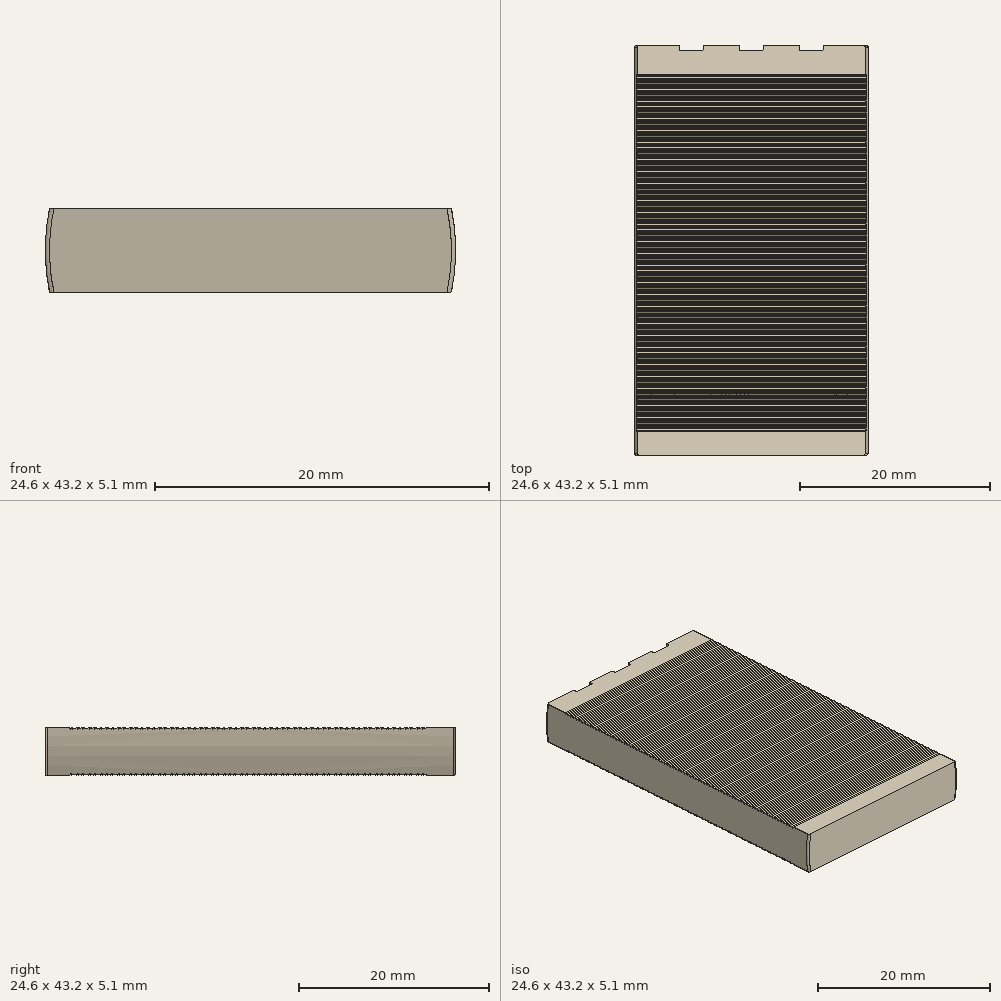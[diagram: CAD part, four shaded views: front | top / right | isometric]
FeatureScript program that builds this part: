
annotation { "Feature Type Name" : "Feature", "Feature Type Description" : "" }
export const myFeature = defineFeature(function(context is Context, id is Id, definition is map)
    precondition{}
    {
        {
            var Q0;
            Q0=qCreatedBy(makeId("Front.planeOp"),FACE);
            var sketch = newSketch(context, id + "F0", { "sketchPlane" : qUnion([Q0])});
            skCircle(sketch, "E0", {"center": v(0, 0) * mm, "radius": 12.32 * mm});
            skSolve(sketch);
        }
        {
            var Q0;
            Q0=qSketchRegion(id+"F0",true);
            extrude(context, id + "F1", {"entities" : qUnion([Q0]), "endBound" : BoundingType.SYMMETRIC, "depth" : 43.18 * mm, "offsetDistance" : 25.4 * mm});
        }
        {
            var Q0;
            Q0=makeQuery(id+"F1.opExtrude","CAP_FACE",FACE,{"disambiguationData":[OSD([sQuery(id+"F0.wireOp",EDGE,"E0")])],"isStart":false});
            var sketch = newSketch(context, id + "F2", { "sketchPlane" : qUnion([Q0])});
            skLineSegment(sketch, "E1.bottom", {"start": v(12.45, 2.54) * mm, "end": v(-12.45, 2.54) * mm});
            skLineSegment(sketch, "E1.top", {"start": v(12.45, -2.54) * mm, "end": v(-12.45, -2.54) * mm});
            skPoint(sketch, "E1.middle", {"position": v(0, 0) * mm});
            skArc(sketch, "E2", {"start": v(-12.45, 2.54) * mm, "mid": v(-12.7, 0) * mm, "end": v(-12.45, -2.54) * mm});
            skArc(sketch, "E3.trimOffspring", {"start": v(12.45, -2.54) * mm, "mid": v(12.7, 0) * mm, "end": v(12.45, 2.54) * mm});
            skSolve(sketch);
        }
        {
            var Q0;
            Q0=qSketchRegion(id+"F2",true);
            extrude(context, id + "F3", {"entities" : qUnion([Q0]), "operationType" : NewBodyOperationType.INTERSECT, "oppositeDirection" : true, "depth" : 50.8 * mm, "offsetDistance" : 25.4 * mm});
        }
        {
            var Q0;
            Q0=qCreatedBy(makeId("Right.planeOp"),FACE);
            var sketch = newSketch(context, id + "F4", { "sketchPlane" : qUnion([Q0])});
            skLineSegment(sketch, "E4", {"start": v(6.35, 2.54) * mm, "end": v(6.22, 2.32) * mm});
            skLineSegment(sketch, "E5", {"start": v(6.22, 2.32) * mm, "end": v(6.1, 2.54) * mm});
            skLineSegment(sketch, "E6.1.0.0", {"start": v(6.1, 2.54) * mm, "end": v(5.97, 2.32) * mm});
            skLineSegment(sketch, "E6.1.0.1", {"start": v(5.97, 2.32) * mm, "end": v(5.84, 2.54) * mm});
            skLineSegment(sketch, "E6.2.0.0", {"start": v(5.84, 2.54) * mm, "end": v(5.72, 2.32) * mm});
            skLineSegment(sketch, "E6.2.0.1", {"start": v(5.72, 2.32) * mm, "end": v(5.59, 2.54) * mm});
            skLineSegment(sketch, "E6.3.0.0", {"start": v(5.59, 2.54) * mm, "end": v(5.46, 2.32) * mm});
            skLineSegment(sketch, "E6.3.0.1", {"start": v(5.46, 2.32) * mm, "end": v(5.33, 2.54) * mm});
            skLineSegment(sketch, "E6.4.0.0", {"start": v(5.33, 2.54) * mm, "end": v(5.2, 2.32) * mm});
            skLineSegment(sketch, "E6.4.0.1", {"start": v(5.2, 2.32) * mm, "end": v(5.08, 2.54) * mm});
            skLineSegment(sketch, "E6.5.0.0", {"start": v(5.08, 2.54) * mm, "end": v(4.95, 2.32) * mm});
            skLineSegment(sketch, "E6.5.0.1", {"start": v(4.95, 2.32) * mm, "end": v(4.83, 2.54) * mm});
            skLineSegment(sketch, "E6.6.0.0", {"start": v(4.83, 2.54) * mm, "end": v(4.7, 2.32) * mm});
            skLineSegment(sketch, "E6.6.0.1", {"start": v(4.7, 2.32) * mm, "end": v(4.57, 2.54) * mm});
            skLineSegment(sketch, "E6.7.0.0", {"start": v(4.57, 2.54) * mm, "end": v(4.45, 2.32) * mm});
            skLineSegment(sketch, "E6.7.0.1", {"start": v(4.45, 2.32) * mm, "end": v(4.32, 2.54) * mm});
            skLineSegment(sketch, "E6.8.0.0", {"start": v(4.32, 2.54) * mm, "end": v(4.2, 2.32) * mm});
            skLineSegment(sketch, "E6.8.0.1", {"start": v(4.2, 2.32) * mm, "end": v(4.06, 2.54) * mm});
            skLineSegment(sketch, "E6.9.0.0", {"start": v(4.06, 2.54) * mm, "end": v(3.94, 2.32) * mm});
            skLineSegment(sketch, "E6.9.0.1", {"start": v(3.94, 2.32) * mm, "end": v(3.81, 2.54) * mm});
            skLineSegment(sketch, "E6.10.0.0", {"start": v(3.81, 2.54) * mm, "end": v(3.68, 2.32) * mm});
            skLineSegment(sketch, "E6.10.0.1", {"start": v(3.68, 2.32) * mm, "end": v(3.56, 2.54) * mm});
            skLineSegment(sketch, "E6.11.0.0", {"start": v(3.56, 2.54) * mm, "end": v(3.43, 2.32) * mm});
            skLineSegment(sketch, "E6.11.0.1", {"start": v(3.43, 2.32) * mm, "end": v(3.3, 2.54) * mm});
            skLineSegment(sketch, "E6.12.0.0", {"start": v(3.3, 2.54) * mm, "end": v(3.18, 2.32) * mm});
            skLineSegment(sketch, "E6.12.0.1", {"start": v(3.17, 2.32) * mm, "end": v(3.05, 2.54) * mm});
            skLineSegment(sketch, "E6.13.0.0", {"start": v(3.05, 2.54) * mm, "end": v(2.92, 2.32) * mm});
            skLineSegment(sketch, "E6.13.0.1", {"start": v(2.92, 2.32) * mm, "end": v(2.8, 2.54) * mm});
            skLineSegment(sketch, "E6.14.0.0", {"start": v(2.8, 2.54) * mm, "end": v(2.67, 2.32) * mm});
            skLineSegment(sketch, "E6.14.0.1", {"start": v(2.67, 2.32) * mm, "end": v(2.54, 2.54) * mm});
            skLineSegment(sketch, "E6.15.0.0", {"start": v(2.54, 2.54) * mm, "end": v(2.41, 2.32) * mm});
            skLineSegment(sketch, "E6.15.0.1", {"start": v(2.41, 2.32) * mm, "end": v(2.29, 2.54) * mm});
            skLineSegment(sketch, "E6.16.0.0", {"start": v(2.29, 2.54) * mm, "end": v(2.16, 2.32) * mm});
            skLineSegment(sketch, "E6.16.0.1", {"start": v(2.16, 2.32) * mm, "end": v(2.03, 2.54) * mm});
            skLineSegment(sketch, "E6.17.0.0", {"start": v(2.03, 2.54) * mm, "end": v(1.9, 2.32) * mm});
            skLineSegment(sketch, "E6.17.0.1", {"start": v(1.9, 2.32) * mm, "end": v(1.78, 2.54) * mm});
            skLineSegment(sketch, "E6.18.0.0", {"start": v(1.78, 2.54) * mm, "end": v(1.65, 2.32) * mm});
            skLineSegment(sketch, "E6.18.0.1", {"start": v(1.65, 2.32) * mm, "end": v(1.52, 2.54) * mm});
            skLineSegment(sketch, "E6.19.0.0", {"start": v(1.52, 2.54) * mm, "end": v(1.4, 2.32) * mm});
            skLineSegment(sketch, "E6.19.0.1", {"start": v(1.4, 2.32) * mm, "end": v(1.27, 2.54) * mm});
            skLineSegment(sketch, "E6.20.0.0", {"start": v(1.27, 2.54) * mm, "end": v(1.14, 2.32) * mm});
            skLineSegment(sketch, "E6.20.0.1", {"start": v(1.14, 2.32) * mm, "end": v(1.02, 2.54) * mm});
            skLineSegment(sketch, "E6.21.0.0", {"start": v(1.02, 2.54) * mm, "end": v(0.89, 2.32) * mm});
            skLineSegment(sketch, "E6.21.0.1", {"start": v(0.89, 2.32) * mm, "end": v(0.76, 2.54) * mm});
            skLineSegment(sketch, "E6.22.0.0", {"start": v(0.76, 2.54) * mm, "end": v(0.63, 2.32) * mm});
            skLineSegment(sketch, "E6.22.0.1", {"start": v(0.63, 2.32) * mm, "end": v(0.5, 2.54) * mm});
            skLineSegment(sketch, "E6.23.0.0", {"start": v(0.5, 2.54) * mm, "end": v(0.38, 2.32) * mm});
            skLineSegment(sketch, "E6.23.0.1", {"start": v(0.38, 2.32) * mm, "end": v(0.25, 2.54) * mm});
            skLineSegment(sketch, "E6.24.0.0", {"start": v(0.25, 2.54) * mm, "end": v(0.13, 2.32) * mm});
            skLineSegment(sketch, "E6.24.0.1", {"start": v(0.13, 2.32) * mm, "end": v(0, 2.54) * mm});
            skLineSegment(sketch, "E6.25.0.0", {"start": v(0, 2.54) * mm, "end": v(-0.13, 2.32) * mm});
            skLineSegment(sketch, "E6.25.0.1", {"start": v(-0.13, 2.32) * mm, "end": v(-0.25, 2.54) * mm});
            skLineSegment(sketch, "E6.26.0.0", {"start": v(-0.25, 2.54) * mm, "end": v(-0.38, 2.32) * mm});
            skLineSegment(sketch, "E6.26.0.1", {"start": v(-0.38, 2.32) * mm, "end": v(-0.5, 2.54) * mm});
            skLineSegment(sketch, "E6.27.0.0", {"start": v(-0.5, 2.54) * mm, "end": v(-0.64, 2.32) * mm});
            skLineSegment(sketch, "E6.27.0.1", {"start": v(-0.64, 2.32) * mm, "end": v(-0.76, 2.54) * mm});
            skLineSegment(sketch, "E6.28.0.0", {"start": v(-0.76, 2.54) * mm, "end": v(-0.89, 2.32) * mm});
            skLineSegment(sketch, "E6.28.0.1", {"start": v(-0.89, 2.32) * mm, "end": v(-1.02, 2.54) * mm});
            skLineSegment(sketch, "E6.29.0.0", {"start": v(-1.02, 2.54) * mm, "end": v(-1.14, 2.32) * mm});
            skLineSegment(sketch, "E6.29.0.1", {"start": v(-1.14, 2.32) * mm, "end": v(-1.27, 2.54) * mm});
            skLineSegment(sketch, "E6.30.0.0", {"start": v(-1.27, 2.54) * mm, "end": v(-1.4, 2.32) * mm});
            skLineSegment(sketch, "E6.30.0.1", {"start": v(-1.4, 2.32) * mm, "end": v(-1.52, 2.54) * mm});
            skLineSegment(sketch, "E6.31.0.0", {"start": v(-1.52, 2.54) * mm, "end": v(-1.65, 2.32) * mm});
            skLineSegment(sketch, "E6.31.0.1", {"start": v(-1.65, 2.32) * mm, "end": v(-1.78, 2.54) * mm});
            skLineSegment(sketch, "E6.32.0.0", {"start": v(-1.78, 2.54) * mm, "end": v(-1.9, 2.32) * mm});
            skLineSegment(sketch, "E6.32.0.1", {"start": v(-1.9, 2.32) * mm, "end": v(-2.03, 2.54) * mm});
            skLineSegment(sketch, "E6.33.0.0", {"start": v(-2.03, 2.54) * mm, "end": v(-2.16, 2.32) * mm});
            skLineSegment(sketch, "E6.33.0.1", {"start": v(-2.16, 2.32) * mm, "end": v(-2.29, 2.54) * mm});
            skLineSegment(sketch, "E6.34.0.0", {"start": v(-2.29, 2.54) * mm, "end": v(-2.41, 2.32) * mm});
            skLineSegment(sketch, "E6.34.0.1", {"start": v(-2.41, 2.32) * mm, "end": v(-2.54, 2.54) * mm});
            skLineSegment(sketch, "E6.35.0.0", {"start": v(-2.54, 2.54) * mm, "end": v(-2.67, 2.32) * mm});
            skLineSegment(sketch, "E6.35.0.1", {"start": v(-2.67, 2.32) * mm, "end": v(-2.8, 2.54) * mm});
            skLineSegment(sketch, "E6.36.0.0", {"start": v(-2.8, 2.54) * mm, "end": v(-2.92, 2.32) * mm});
            skLineSegment(sketch, "E6.36.0.1", {"start": v(-2.92, 2.32) * mm, "end": v(-3.05, 2.54) * mm});
            skLineSegment(sketch, "E6.37.0.0", {"start": v(-3.05, 2.54) * mm, "end": v(-3.18, 2.32) * mm});
            skLineSegment(sketch, "E6.37.0.1", {"start": v(-3.18, 2.32) * mm, "end": v(-3.3, 2.54) * mm});
            skLineSegment(sketch, "E6.38.0.0", {"start": v(-3.3, 2.54) * mm, "end": v(-3.43, 2.32) * mm});
            skLineSegment(sketch, "E6.38.0.1", {"start": v(-3.43, 2.32) * mm, "end": v(-3.56, 2.54) * mm});
            skLineSegment(sketch, "E6.39.0.0", {"start": v(-3.56, 2.54) * mm, "end": v(-3.68, 2.32) * mm});
            skLineSegment(sketch, "E6.39.0.1", {"start": v(-3.68, 2.32) * mm, "end": v(-3.81, 2.54) * mm});
            skLineSegment(sketch, "E6.40.0.0", {"start": v(-3.81, 2.54) * mm, "end": v(-3.94, 2.32) * mm});
            skLineSegment(sketch, "E6.40.0.1", {"start": v(-3.94, 2.32) * mm, "end": v(-4.06, 2.54) * mm});
            skLineSegment(sketch, "E6.41.0.0", {"start": v(-4.06, 2.54) * mm, "end": v(-4.2, 2.32) * mm});
            skLineSegment(sketch, "E6.41.0.1", {"start": v(-4.2, 2.32) * mm, "end": v(-4.32, 2.54) * mm});
            skLineSegment(sketch, "E6.42.0.0", {"start": v(-4.32, 2.54) * mm, "end": v(-4.45, 2.32) * mm});
            skLineSegment(sketch, "E6.42.0.1", {"start": v(-4.45, 2.32) * mm, "end": v(-4.57, 2.54) * mm});
            skLineSegment(sketch, "E6.43.0.0", {"start": v(-4.57, 2.54) * mm, "end": v(-4.7, 2.32) * mm});
            skLineSegment(sketch, "E6.43.0.1", {"start": v(-4.7, 2.32) * mm, "end": v(-4.83, 2.54) * mm});
            skLineSegment(sketch, "E6.44.0.0", {"start": v(-4.83, 2.54) * mm, "end": v(-4.95, 2.32) * mm});
            skLineSegment(sketch, "E6.44.0.1", {"start": v(-4.95, 2.32) * mm, "end": v(-5.08, 2.54) * mm});
            skLineSegment(sketch, "E6.45.0.0", {"start": v(-5.08, 2.54) * mm, "end": v(-5.2, 2.32) * mm});
            skLineSegment(sketch, "E6.45.0.1", {"start": v(-5.2, 2.32) * mm, "end": v(-5.33, 2.54) * mm});
            skLineSegment(sketch, "E6.46.0.0", {"start": v(-5.33, 2.54) * mm, "end": v(-5.46, 2.32) * mm});
            skLineSegment(sketch, "E6.46.0.1", {"start": v(-5.46, 2.32) * mm, "end": v(-5.59, 2.54) * mm});
            skLineSegment(sketch, "E6.47.0.0", {"start": v(-5.59, 2.54) * mm, "end": v(-5.72, 2.32) * mm});
            skLineSegment(sketch, "E6.47.0.1", {"start": v(-5.72, 2.32) * mm, "end": v(-5.84, 2.54) * mm});
            skLineSegment(sketch, "E6.48.0.0", {"start": v(-5.84, 2.54) * mm, "end": v(-5.97, 2.32) * mm});
            skLineSegment(sketch, "E6.48.0.1", {"start": v(-5.97, 2.32) * mm, "end": v(-6.1, 2.54) * mm});
            skLineSegment(sketch, "E6.49.0.0", {"start": v(-6.1, 2.54) * mm, "end": v(-6.22, 2.32) * mm});
            skLineSegment(sketch, "E6.49.0.1", {"start": v(-6.22, 2.32) * mm, "end": v(-6.35, 2.54) * mm});
            skLineSegment(sketch, "E6.50.0.0", {"start": v(-6.35, 2.54) * mm, "end": v(-6.48, 2.32) * mm});
            skLineSegment(sketch, "E6.50.0.1", {"start": v(-6.48, 2.32) * mm, "end": v(-6.6, 2.54) * mm});
            skLineSegment(sketch, "E6.51.0.0", {"start": v(-6.6, 2.54) * mm, "end": v(-6.73, 2.32) * mm});
            skLineSegment(sketch, "E6.51.0.1", {"start": v(-6.73, 2.32) * mm, "end": v(-6.86, 2.54) * mm});
            skLineSegment(sketch, "E6.52.0.0", {"start": v(-6.86, 2.54) * mm, "end": v(-6.99, 2.32) * mm});
            skLineSegment(sketch, "E6.52.0.1", {"start": v(-6.99, 2.32) * mm, "end": v(-7.11, 2.54) * mm});
            skLineSegment(sketch, "E6.53.0.0", {"start": v(-7.11, 2.54) * mm, "end": v(-7.24, 2.32) * mm});
            skLineSegment(sketch, "E6.53.0.1", {"start": v(-7.24, 2.32) * mm, "end": v(-7.37, 2.54) * mm});
            skLineSegment(sketch, "E6.54.0.0", {"start": v(-7.37, 2.54) * mm, "end": v(-7.5, 2.32) * mm});
            skLineSegment(sketch, "E6.54.0.1", {"start": v(-7.5, 2.32) * mm, "end": v(-7.62, 2.54) * mm});
            skLineSegment(sketch, "E6.55.0.0", {"start": v(-7.62, 2.54) * mm, "end": v(-7.75, 2.32) * mm});
            skLineSegment(sketch, "E6.55.0.1", {"start": v(-7.75, 2.32) * mm, "end": v(-7.87, 2.54) * mm});
            skLineSegment(sketch, "E6.56.0.0", {"start": v(-7.87, 2.54) * mm, "end": v(-8, 2.32) * mm});
            skLineSegment(sketch, "E6.56.0.1", {"start": v(-8, 2.32) * mm, "end": v(-8.13, 2.54) * mm});
            skLineSegment(sketch, "E6.57.0.0", {"start": v(-8.13, 2.54) * mm, "end": v(-8.26, 2.32) * mm});
            skLineSegment(sketch, "E6.57.0.1", {"start": v(-8.26, 2.32) * mm, "end": v(-8.38, 2.54) * mm});
            skLineSegment(sketch, "E6.58.0.0", {"start": v(-8.38, 2.54) * mm, "end": v(-8.5, 2.32) * mm});
            skLineSegment(sketch, "E6.58.0.1", {"start": v(-8.5, 2.32) * mm, "end": v(-8.64, 2.54) * mm});
            skLineSegment(sketch, "E6.59.0.0", {"start": v(-8.64, 2.54) * mm, "end": v(-8.76, 2.32) * mm});
            skLineSegment(sketch, "E6.59.0.1", {"start": v(-8.76, 2.32) * mm, "end": v(-8.9, 2.54) * mm});
            skLineSegment(sketch, "E6.60.0.0", {"start": v(-8.9, 2.54) * mm, "end": v(-9.02, 2.32) * mm});
            skLineSegment(sketch, "E6.60.0.1", {"start": v(-9.02, 2.32) * mm, "end": v(-9.14, 2.54) * mm});
            skLineSegment(sketch, "E6.61.0.0", {"start": v(-9.14, 2.54) * mm, "end": v(-9.27, 2.32) * mm});
            skLineSegment(sketch, "E6.61.0.1", {"start": v(-9.27, 2.32) * mm, "end": v(-9.4, 2.54) * mm});
            skLineSegment(sketch, "E6.62.0.0", {"start": v(-9.4, 2.54) * mm, "end": v(-9.53, 2.32) * mm});
            skLineSegment(sketch, "E6.62.0.1", {"start": v(-9.53, 2.32) * mm, "end": v(-9.65, 2.54) * mm});
            skLineSegment(sketch, "E6.63.0.0", {"start": v(-9.65, 2.54) * mm, "end": v(-9.78, 2.32) * mm});
            skLineSegment(sketch, "E6.63.0.1", {"start": v(-9.78, 2.32) * mm, "end": v(-9.9, 2.54) * mm});
            skLineSegment(sketch, "E6.64.0.0", {"start": v(-9.9, 2.54) * mm, "end": v(-10.03, 2.32) * mm});
            skLineSegment(sketch, "E6.64.0.1", {"start": v(-10.03, 2.32) * mm, "end": v(-10.16, 2.54) * mm});
            skLineSegment(sketch, "E6.65.0.0", {"start": v(-10.16, 2.54) * mm, "end": v(-10.29, 2.32) * mm});
            skLineSegment(sketch, "E6.65.0.1", {"start": v(-10.29, 2.32) * mm, "end": v(-10.41, 2.54) * mm});
            skLineSegment(sketch, "E6.66.0.0", {"start": v(-10.41, 2.54) * mm, "end": v(-10.54, 2.32) * mm});
            skLineSegment(sketch, "E6.66.0.1", {"start": v(-10.54, 2.32) * mm, "end": v(-10.67, 2.54) * mm});
            skLineSegment(sketch, "E6.67.0.0", {"start": v(-10.67, 2.54) * mm, "end": v(-10.8, 2.32) * mm});
            skLineSegment(sketch, "E6.67.0.1", {"start": v(-10.8, 2.32) * mm, "end": v(-10.92, 2.54) * mm});
            skLineSegment(sketch, "E6.68.0.0", {"start": v(-10.92, 2.54) * mm, "end": v(-11.05, 2.32) * mm});
            skLineSegment(sketch, "E6.68.0.1", {"start": v(-11.05, 2.32) * mm, "end": v(-11.18, 2.54) * mm});
            skLineSegment(sketch, "E6.69.0.0", {"start": v(-11.18, 2.54) * mm, "end": v(-11.3, 2.32) * mm});
            skLineSegment(sketch, "E6.69.0.1", {"start": v(-11.3, 2.32) * mm, "end": v(-11.43, 2.54) * mm});
            skLineSegment(sketch, "E6.70.0.0", {"start": v(-11.43, 2.54) * mm, "end": v(-11.56, 2.32) * mm});
            skLineSegment(sketch, "E6.70.0.1", {"start": v(-11.56, 2.32) * mm, "end": v(-11.68, 2.54) * mm});
            skLineSegment(sketch, "E6.71.0.0", {"start": v(-11.68, 2.54) * mm, "end": v(-11.81, 2.32) * mm});
            skLineSegment(sketch, "E6.71.0.1", {"start": v(-11.81, 2.32) * mm, "end": v(-11.94, 2.54) * mm});
            skLineSegment(sketch, "E6.72.0.0", {"start": v(-11.94, 2.54) * mm, "end": v(-12.07, 2.32) * mm});
            skLineSegment(sketch, "E6.72.0.1", {"start": v(-12.07, 2.32) * mm, "end": v(-12.2, 2.54) * mm});
            skLineSegment(sketch, "E6.73.0.0", {"start": v(-12.2, 2.54) * mm, "end": v(-12.32, 2.32) * mm});
            skLineSegment(sketch, "E6.73.0.1", {"start": v(-12.32, 2.32) * mm, "end": v(-12.45, 2.54) * mm});
            skLineSegment(sketch, "E6.74.0.0", {"start": v(-12.45, 2.54) * mm, "end": v(-12.57, 2.32) * mm});
            skLineSegment(sketch, "E6.74.0.1", {"start": v(-12.57, 2.32) * mm, "end": v(-12.7, 2.54) * mm});
            skLineSegment(sketch, "E6.75.0.0", {"start": v(-12.7, 2.54) * mm, "end": v(-12.83, 2.32) * mm});
            skLineSegment(sketch, "E6.75.0.1", {"start": v(-12.83, 2.32) * mm, "end": v(-12.95, 2.54) * mm});
            skLineSegment(sketch, "E6.76.0.0", {"start": v(-12.95, 2.54) * mm, "end": v(-13.08, 2.32) * mm});
            skLineSegment(sketch, "E6.76.0.1", {"start": v(-13.08, 2.32) * mm, "end": v(-13.2, 2.54) * mm});
            skLineSegment(sketch, "E6.77.0.0", {"start": v(-13.2, 2.54) * mm, "end": v(-13.34, 2.32) * mm});
            skLineSegment(sketch, "E6.77.0.1", {"start": v(-13.34, 2.32) * mm, "end": v(-13.46, 2.54) * mm});
            skLineSegment(sketch, "E6.78.0.0", {"start": v(-13.46, 2.54) * mm, "end": v(-13.59, 2.32) * mm});
            skLineSegment(sketch, "E6.78.0.1", {"start": v(-13.59, 2.32) * mm, "end": v(-13.72, 2.54) * mm});
            skLineSegment(sketch, "E6.79.0.0", {"start": v(-13.72, 2.54) * mm, "end": v(-13.84, 2.32) * mm});
            skLineSegment(sketch, "E6.79.0.1", {"start": v(-13.84, 2.32) * mm, "end": v(-13.97, 2.54) * mm});
            skLineSegment(sketch, "E6.80.0.0", {"start": v(-13.97, 2.54) * mm, "end": v(-14.1, 2.32) * mm});
            skLineSegment(sketch, "E6.80.0.1", {"start": v(-14.1, 2.32) * mm, "end": v(-14.22, 2.54) * mm});
            skLineSegment(sketch, "E6.81.0.0", {"start": v(-14.22, 2.54) * mm, "end": v(-14.35, 2.32) * mm});
            skLineSegment(sketch, "E6.81.0.1", {"start": v(-14.35, 2.32) * mm, "end": v(-14.48, 2.54) * mm});
            skLineSegment(sketch, "E6.82.0.0", {"start": v(-14.48, 2.54) * mm, "end": v(-14.6, 2.32) * mm});
            skLineSegment(sketch, "E6.82.0.1", {"start": v(-14.6, 2.32) * mm, "end": v(-14.73, 2.54) * mm});
            skLineSegment(sketch, "E6.83.0.0", {"start": v(-14.73, 2.54) * mm, "end": v(-14.86, 2.32) * mm});
            skLineSegment(sketch, "E6.83.0.1", {"start": v(-14.86, 2.32) * mm, "end": v(-14.99, 2.54) * mm});
            skLineSegment(sketch, "E6.84.0.0", {"start": v(-14.99, 2.54) * mm, "end": v(-15.11, 2.32) * mm});
            skLineSegment(sketch, "E6.84.0.1", {"start": v(-15.11, 2.32) * mm, "end": v(-15.24, 2.54) * mm});
            skLineSegment(sketch, "E6.85.0.0", {"start": v(-15.24, 2.54) * mm, "end": v(-15.37, 2.32) * mm});
            skLineSegment(sketch, "E6.85.0.1", {"start": v(-15.37, 2.32) * mm, "end": v(-15.5, 2.54) * mm});
            skLineSegment(sketch, "E6.86.0.0", {"start": v(-15.5, 2.54) * mm, "end": v(-15.62, 2.32) * mm});
            skLineSegment(sketch, "E6.86.0.1", {"start": v(-15.62, 2.32) * mm, "end": v(-15.75, 2.54) * mm});
            skLineSegment(sketch, "E6.87.0.0", {"start": v(-15.75, 2.54) * mm, "end": v(-15.88, 2.32) * mm});
            skLineSegment(sketch, "E6.87.0.1", {"start": v(-15.88, 2.32) * mm, "end": v(-16, 2.54) * mm});
            skLineSegment(sketch, "E6.88.0.0", {"start": v(-16, 2.54) * mm, "end": v(-16.13, 2.32) * mm});
            skLineSegment(sketch, "E6.88.0.1", {"start": v(-16.13, 2.32) * mm, "end": v(-16.26, 2.54) * mm});
            skLineSegment(sketch, "E6.89.0.0", {"start": v(-16.26, 2.54) * mm, "end": v(-16.38, 2.32) * mm});
            skLineSegment(sketch, "E6.89.0.1", {"start": v(-16.38, 2.32) * mm, "end": v(-16.51, 2.54) * mm});
            skLineSegment(sketch, "E6.90.0.0", {"start": v(-16.51, 2.54) * mm, "end": v(-16.64, 2.32) * mm});
            skLineSegment(sketch, "E6.90.0.1", {"start": v(-16.64, 2.32) * mm, "end": v(-16.76, 2.54) * mm});
            skLineSegment(sketch, "E6.91.0.0", {"start": v(-16.76, 2.54) * mm, "end": v(-16.9, 2.32) * mm});
            skLineSegment(sketch, "E6.91.0.1", {"start": v(-16.9, 2.32) * mm, "end": v(-17.02, 2.54) * mm});
            skLineSegment(sketch, "E6.92.0.0", {"start": v(-17.02, 2.54) * mm, "end": v(-17.15, 2.32) * mm});
            skLineSegment(sketch, "E6.92.0.1", {"start": v(-17.15, 2.32) * mm, "end": v(-17.27, 2.54) * mm});
            skLineSegment(sketch, "E6.93.0.0", {"start": v(-17.27, 2.54) * mm, "end": v(-17.4, 2.32) * mm});
            skLineSegment(sketch, "E6.93.0.1", {"start": v(-17.4, 2.32) * mm, "end": v(-17.53, 2.54) * mm});
            skLineSegment(sketch, "E6.94.0.0", {"start": v(-17.53, 2.54) * mm, "end": v(-17.65, 2.32) * mm});
            skLineSegment(sketch, "E6.94.0.1", {"start": v(-17.65, 2.32) * mm, "end": v(-17.78, 2.54) * mm});
            skLineSegment(sketch, "E6.95.0.0", {"start": v(-17.78, 2.54) * mm, "end": v(-17.9, 2.32) * mm});
            skLineSegment(sketch, "E6.95.0.1", {"start": v(-17.9, 2.32) * mm, "end": v(-18.03, 2.54) * mm});
            skLineSegment(sketch, "E6.96.0.0", {"start": v(-18.03, 2.54) * mm, "end": v(-18.16, 2.32) * mm});
            skLineSegment(sketch, "E6.96.0.1", {"start": v(-18.16, 2.32) * mm, "end": v(-18.29, 2.54) * mm});
            skLineSegment(sketch, "E6.97.0.0", {"start": v(-18.29, 2.54) * mm, "end": v(-18.42, 2.32) * mm});
            skLineSegment(sketch, "E6.97.0.1", {"start": v(-18.42, 2.32) * mm, "end": v(-18.54, 2.54) * mm});
            skLineSegment(sketch, "E6.98.0.0", {"start": v(-18.54, 2.54) * mm, "end": v(-18.67, 2.32) * mm});
            skLineSegment(sketch, "E6.98.0.1", {"start": v(-18.67, 2.32) * mm, "end": v(-18.8, 2.54) * mm});
            skLineSegment(sketch, "E6.99.0.0", {"start": v(-18.8, 2.54) * mm, "end": v(-18.92, 2.32) * mm});
            skLineSegment(sketch, "E6.99.0.1", {"start": v(-18.92, 2.32) * mm, "end": v(-19.05, 2.54) * mm});
            skLineSegment(sketch, "E6.direction1", {"start": v(6.22, -2.33) * mm, "end": v(5.97, -2.33) * mm, "construction": true});
            skLineSegment(sketch, "E7", {"start": v(-19.05, 2.6) * mm, "end": v(-19.05, 2.54) * mm});
            skLineSegment(sketch, "E8.MirrorCS", {"start": v(6.22, -2.33) * mm, "end": v(6.1, -2.55) * mm});
            skLineSegment(sketch, "E9.MirrorCS", {"start": v(6.35, -2.55) * mm, "end": v(6.22, -2.33) * mm});
            skLineSegment(sketch, "E10.MirrorCS", {"start": v(5.97, -2.33) * mm, "end": v(5.84, -2.55) * mm});
            skLineSegment(sketch, "E11.MirrorCS", {"start": v(-19.05, -2.6) * mm, "end": v(-19.05, -2.55) * mm});
            skLineSegment(sketch, "E12.MirrorCS", {"start": v(6.1, -2.55) * mm, "end": v(5.97, -2.33) * mm});
            skLineSegment(sketch, "E13.MirrorCS", {"start": v(-11.05, -2.33) * mm, "end": v(-11.18, -2.55) * mm});
            skLineSegment(sketch, "E14.MirrorCS", {"start": v(4.83, -2.55) * mm, "end": v(4.7, -2.33) * mm});
            skLineSegment(sketch, "E15.MirrorCS", {"start": v(-2.29, -2.55) * mm, "end": v(-2.41, -2.33) * mm});
            skLineSegment(sketch, "E16.MirrorCS", {"start": v(-18.54, -2.55) * mm, "end": v(-18.67, -2.33) * mm});
            skLineSegment(sketch, "E17.MirrorCS", {"start": v(-14.48, -2.55) * mm, "end": v(-14.6, -2.33) * mm});
            skLineSegment(sketch, "E18.MirrorCS", {"start": v(-16.76, -2.55) * mm, "end": v(-16.9, -2.33) * mm});
            skLineSegment(sketch, "E19.MirrorCS", {"start": v(-0.64, -2.33) * mm, "end": v(-0.76, -2.55) * mm});
            skLineSegment(sketch, "E20.MirrorCS", {"start": v(-8.76, -2.33) * mm, "end": v(-8.9, -2.55) * mm});
            skLineSegment(sketch, "E21.MirrorCS", {"start": v(-2.67, -2.33) * mm, "end": v(-2.8, -2.55) * mm});
            skLineSegment(sketch, "E22.MirrorCS", {"start": v(-15.11, -2.33) * mm, "end": v(-15.24, -2.55) * mm});
            skLineSegment(sketch, "E23.MirrorCS", {"start": v(2.29, -2.55) * mm, "end": v(2.16, -2.33) * mm});
            skLineSegment(sketch, "E24.MirrorCS", {"start": v(-14.99, -2.55) * mm, "end": v(-15.11, -2.33) * mm});
            skLineSegment(sketch, "E25.MirrorCS", {"start": v(-11.68, -2.55) * mm, "end": v(-11.81, -2.33) * mm});
            skLineSegment(sketch, "E26.MirrorCS", {"start": v(2.8, -2.55) * mm, "end": v(2.67, -2.33) * mm});
            skLineSegment(sketch, "E27.MirrorCS", {"start": v(2.03, -2.55) * mm, "end": v(1.9, -2.33) * mm});
            skLineSegment(sketch, "E28.MirrorCS", {"start": v(-3.43, -2.33) * mm, "end": v(-3.56, -2.55) * mm});
            skLineSegment(sketch, "E29.MirrorCS", {"start": v(-2.16, -2.33) * mm, "end": v(-2.29, -2.55) * mm});
            skLineSegment(sketch, "E30.MirrorCS", {"start": v(-14.35, -2.33) * mm, "end": v(-14.48, -2.55) * mm});
            skLineSegment(sketch, "E31.MirrorCS", {"start": v(-12.7, -2.55) * mm, "end": v(-12.83, -2.33) * mm});
            skLineSegment(sketch, "E32.MirrorCS", {"start": v(-8.38, -2.55) * mm, "end": v(-8.5, -2.33) * mm});
            skLineSegment(sketch, "E33.MirrorCS", {"start": v(-11.56, -2.33) * mm, "end": v(-11.68, -2.55) * mm});
            skLineSegment(sketch, "E34.MirrorCS", {"start": v(-17.65, -2.33) * mm, "end": v(-17.78, -2.55) * mm});
            skLineSegment(sketch, "E35.MirrorCS", {"start": v(-12.32, -2.33) * mm, "end": v(-12.45, -2.55) * mm});
            skLineSegment(sketch, "E36.MirrorCS", {"start": v(2.16, -2.33) * mm, "end": v(2.03, -2.55) * mm});
            skLineSegment(sketch, "E37.MirrorCS", {"start": v(-2.8, -2.55) * mm, "end": v(-2.92, -2.33) * mm});
            skLineSegment(sketch, "E38.MirrorCS", {"start": v(-4.57, -2.55) * mm, "end": v(-4.7, -2.33) * mm});
            skLineSegment(sketch, "E39.MirrorCS", {"start": v(-1.02, -2.55) * mm, "end": v(-1.14, -2.33) * mm});
            skLineSegment(sketch, "E40.MirrorCS", {"start": v(4.95, -2.33) * mm, "end": v(4.83, -2.55) * mm});
            skLineSegment(sketch, "E41.MirrorCS", {"start": v(5.08, -2.55) * mm, "end": v(4.95, -2.33) * mm});
            skLineSegment(sketch, "E42.MirrorCS", {"start": v(-13.46, -2.55) * mm, "end": v(-13.59, -2.33) * mm});
            skLineSegment(sketch, "E43.MirrorCS", {"start": v(-13.08, -2.33) * mm, "end": v(-13.2, -2.55) * mm});
            skLineSegment(sketch, "E44.MirrorCS", {"start": v(-5.59, -2.55) * mm, "end": v(-5.72, -2.33) * mm});
            skLineSegment(sketch, "E45.MirrorCS", {"start": v(-5.33, -2.55) * mm, "end": v(-5.46, -2.33) * mm});
            skLineSegment(sketch, "E46.MirrorCS", {"start": v(4.45, -2.33) * mm, "end": v(4.32, -2.55) * mm});
            skLineSegment(sketch, "E47.MirrorCS", {"start": v(-3.56, -2.55) * mm, "end": v(-3.68, -2.33) * mm});
            skLineSegment(sketch, "E48.MirrorCS", {"start": v(-15.24, -2.55) * mm, "end": v(-15.37, -2.33) * mm});
            skLineSegment(sketch, "E49.MirrorCS", {"start": v(-6.99, -2.33) * mm, "end": v(-7.11, -2.55) * mm});
            skLineSegment(sketch, "E50.MirrorCS", {"start": v(-2.54, -2.55) * mm, "end": v(-2.67, -2.33) * mm});
            skLineSegment(sketch, "E51.MirrorCS", {"start": v(-12.45, -2.55) * mm, "end": v(-12.57, -2.33) * mm});
            skLineSegment(sketch, "E52.MirrorCS", {"start": v(-16.9, -2.33) * mm, "end": v(-17.02, -2.55) * mm});
            skLineSegment(sketch, "E53.MirrorCS", {"start": v(-3.05, -2.55) * mm, "end": v(-3.18, -2.33) * mm});
            skLineSegment(sketch, "E54.MirrorCS", {"start": v(3.81, -2.55) * mm, "end": v(3.68, -2.33) * mm});
            skLineSegment(sketch, "E55.MirrorCS", {"start": v(-10.67, -2.55) * mm, "end": v(-10.8, -2.33) * mm});
            skLineSegment(sketch, "E56.MirrorCS", {"start": v(-14.22, -2.55) * mm, "end": v(-14.35, -2.33) * mm});
            skLineSegment(sketch, "E57.MirrorCS", {"start": v(-3.94, -2.33) * mm, "end": v(-4.06, -2.55) * mm});
            skLineSegment(sketch, "E58.MirrorCS", {"start": v(-14.1, -2.33) * mm, "end": v(-14.22, -2.55) * mm});
            skLineSegment(sketch, "E59.MirrorCS", {"start": v(-15.5, -2.55) * mm, "end": v(-15.62, -2.33) * mm});
            skLineSegment(sketch, "E60.MirrorCS", {"start": v(3.05, -2.55) * mm, "end": v(2.92, -2.33) * mm});
            skLineSegment(sketch, "E61.MirrorCS", {"start": v(-10.03, -2.33) * mm, "end": v(-10.16, -2.55) * mm});
            skLineSegment(sketch, "E62.MirrorCS", {"start": v(5.84, -2.55) * mm, "end": v(5.72, -2.33) * mm});
            skLineSegment(sketch, "E63.MirrorCS", {"start": v(3.68, -2.33) * mm, "end": v(3.56, -2.55) * mm});
            skLineSegment(sketch, "E64.MirrorCS", {"start": v(-17.53, -2.55) * mm, "end": v(-17.65, -2.33) * mm});
            skLineSegment(sketch, "E65.MirrorCS", {"start": v(1.65, -2.33) * mm, "end": v(1.52, -2.55) * mm});
            skLineSegment(sketch, "E66.MirrorCS", {"start": v(-17.15, -2.33) * mm, "end": v(-17.27, -2.55) * mm});
            skLineSegment(sketch, "E67.MirrorCS", {"start": v(-16.51, -2.55) * mm, "end": v(-16.64, -2.33) * mm});
            skLineSegment(sketch, "E68.MirrorCS", {"start": v(-0.5, -2.55) * mm, "end": v(-0.64, -2.33) * mm});
            skLineSegment(sketch, "E69.MirrorCS", {"start": v(-1.78, -2.55) * mm, "end": v(-1.9, -2.33) * mm});
            skLineSegment(sketch, "E70.MirrorCS", {"start": v(2.92, -2.33) * mm, "end": v(2.8, -2.55) * mm});
            skLineSegment(sketch, "E71.MirrorCS", {"start": v(1.78, -2.55) * mm, "end": v(1.65, -2.33) * mm});
            skLineSegment(sketch, "E72.MirrorCS", {"start": v(-11.94, -2.55) * mm, "end": v(-12.07, -2.33) * mm});
            skLineSegment(sketch, "E73.MirrorCS", {"start": v(-8, -2.33) * mm, "end": v(-8.13, -2.55) * mm});
            skLineSegment(sketch, "E74.MirrorCS", {"start": v(-5.97, -2.33) * mm, "end": v(-6.1, -2.55) * mm});
            skLineSegment(sketch, "E75.MirrorCS", {"start": v(-9.78, -2.33) * mm, "end": v(-9.9, -2.55) * mm});
            skLineSegment(sketch, "E76.MirrorCS", {"start": v(3.3, -2.55) * mm, "end": v(3.18, -2.33) * mm});
            skLineSegment(sketch, "E77.MirrorCS", {"start": v(4.7, -2.33) * mm, "end": v(4.57, -2.55) * mm});
            skLineSegment(sketch, "E78.MirrorCS", {"start": v(-8.5, -2.33) * mm, "end": v(-8.64, -2.55) * mm});
            skLineSegment(sketch, "E79.MirrorCS", {"start": v(1.14, -2.33) * mm, "end": v(1.02, -2.55) * mm});
            skLineSegment(sketch, "E80.MirrorCS", {"start": v(-5.08, -2.55) * mm, "end": v(-5.2, -2.33) * mm});
            skLineSegment(sketch, "E81.MirrorCS", {"start": v(3.94, -2.33) * mm, "end": v(3.81, -2.55) * mm});
            skLineSegment(sketch, "E82.MirrorCS", {"start": v(-12.95, -2.55) * mm, "end": v(-13.08, -2.33) * mm});
            skLineSegment(sketch, "E83.MirrorCS", {"start": v(-3.68, -2.33) * mm, "end": v(-3.81, -2.55) * mm});
            skLineSegment(sketch, "E84.MirrorCS", {"start": v(-16.38, -2.33) * mm, "end": v(-16.51, -2.55) * mm});
            skLineSegment(sketch, "E85.MirrorCS", {"start": v(-2.41, -2.33) * mm, "end": v(-2.54, -2.55) * mm});
            skLineSegment(sketch, "E86.MirrorCS", {"start": v(-1.9, -2.33) * mm, "end": v(-2.03, -2.55) * mm});
            skLineSegment(sketch, "E87.MirrorCS", {"start": v(-10.54, -2.33) * mm, "end": v(-10.67, -2.55) * mm});
            skLineSegment(sketch, "E88.MirrorCS", {"start": v(-3.3, -2.55) * mm, "end": v(-3.43, -2.33) * mm});
            skLineSegment(sketch, "E89.MirrorCS", {"start": v(0.25, -2.55) * mm, "end": v(0.13, -2.33) * mm});
            skLineSegment(sketch, "E90.MirrorCS", {"start": v(-2.92, -2.33) * mm, "end": v(-3.05, -2.55) * mm});
            skLineSegment(sketch, "E91.MirrorCS", {"start": v(-3.18, -2.33) * mm, "end": v(-3.3, -2.55) * mm});
            skLineSegment(sketch, "E92.MirrorCS", {"start": v(0.89, -2.33) * mm, "end": v(0.76, -2.55) * mm});
            skLineSegment(sketch, "E93.MirrorCS", {"start": v(-6.22, -2.33) * mm, "end": v(-6.35, -2.55) * mm});
            skLineSegment(sketch, "E94.MirrorCS", {"start": v(-15.62, -2.33) * mm, "end": v(-15.75, -2.55) * mm});
            skLineSegment(sketch, "E95.MirrorCS", {"start": v(-13.97, -2.55) * mm, "end": v(-14.1, -2.33) * mm});
            skLineSegment(sketch, "E96.MirrorCS", {"start": v(-16.64, -2.33) * mm, "end": v(-16.76, -2.55) * mm});
            skLineSegment(sketch, "E97.MirrorCS", {"start": v(-15.37, -2.33) * mm, "end": v(-15.5, -2.55) * mm});
            skLineSegment(sketch, "E98.MirrorCS", {"start": v(-11.3, -2.33) * mm, "end": v(-11.43, -2.55) * mm});
            skLineSegment(sketch, "E99.MirrorCS", {"start": v(-6.35, -2.55) * mm, "end": v(-6.48, -2.33) * mm});
            skLineSegment(sketch, "E100.MirrorCS", {"start": v(-7.24, -2.33) * mm, "end": v(-7.37, -2.55) * mm});
            skLineSegment(sketch, "E101.MirrorCS", {"start": v(3.17, -2.33) * mm, "end": v(3.05, -2.55) * mm});
            skLineSegment(sketch, "E102.MirrorCS", {"start": v(-10.8, -2.33) * mm, "end": v(-10.92, -2.55) * mm});
            skLineSegment(sketch, "E103.MirrorCS", {"start": v(-8.64, -2.55) * mm, "end": v(-8.76, -2.33) * mm});
            skLineSegment(sketch, "E104.MirrorCS", {"start": v(-11.81, -2.33) * mm, "end": v(-11.94, -2.55) * mm});
            skLineSegment(sketch, "E105.MirrorCS", {"start": v(-7.75, -2.33) * mm, "end": v(-7.87, -2.55) * mm});
            skLineSegment(sketch, "E106.MirrorCS", {"start": v(-17.02, -2.55) * mm, "end": v(-17.15, -2.33) * mm});
            skLineSegment(sketch, "E107.MirrorCS", {"start": v(4.2, -2.33) * mm, "end": v(4.06, -2.55) * mm});
            skLineSegment(sketch, "E108.MirrorCS", {"start": v(-12.83, -2.33) * mm, "end": v(-12.95, -2.55) * mm});
            skLineSegment(sketch, "E109.MirrorCS", {"start": v(-9.4, -2.55) * mm, "end": v(-9.53, -2.33) * mm});
            skLineSegment(sketch, "E110.MirrorCS", {"start": v(-8.13, -2.55) * mm, "end": v(-8.26, -2.33) * mm});
            skLineSegment(sketch, "E111.MirrorCS", {"start": v(-18.03, -2.55) * mm, "end": v(-18.16, -2.33) * mm});
            skLineSegment(sketch, "E112.MirrorCS", {"start": v(-15.88, -2.33) * mm, "end": v(-16, -2.55) * mm});
            skLineSegment(sketch, "E113.MirrorCS", {"start": v(-10.41, -2.55) * mm, "end": v(-10.54, -2.33) * mm});
            skLineSegment(sketch, "E114.MirrorCS", {"start": v(-4.45, -2.33) * mm, "end": v(-4.57, -2.55) * mm});
            skLineSegment(sketch, "E115.MirrorCS", {"start": v(-3.81, -2.55) * mm, "end": v(-3.94, -2.33) * mm});
            skLineSegment(sketch, "E116.MirrorCS", {"start": v(-9.02, -2.33) * mm, "end": v(-9.14, -2.55) * mm});
            skLineSegment(sketch, "E117.MirrorCS", {"start": v(-4.7, -2.33) * mm, "end": v(-4.83, -2.55) * mm});
            skLineSegment(sketch, "E118.MirrorCS", {"start": v(-0.13, -2.33) * mm, "end": v(-0.25, -2.55) * mm});
            skLineSegment(sketch, "E119.MirrorCS", {"start": v(-9.53, -2.33) * mm, "end": v(-9.65, -2.55) * mm});
            skLineSegment(sketch, "E120.MirrorCS", {"start": v(0.76, -2.55) * mm, "end": v(0.63, -2.33) * mm});
            skLineSegment(sketch, "E121.MirrorCS", {"start": v(-1.14, -2.33) * mm, "end": v(-1.27, -2.55) * mm});
            skLineSegment(sketch, "E122.MirrorCS", {"start": v(0.38, -2.33) * mm, "end": v(0.25, -2.55) * mm});
            skLineSegment(sketch, "E123.MirrorCS", {"start": v(-18.16, -2.33) * mm, "end": v(-18.29, -2.55) * mm});
            skLineSegment(sketch, "E124.MirrorCS", {"start": v(-9.14, -2.55) * mm, "end": v(-9.27, -2.33) * mm});
            skLineSegment(sketch, "E125.MirrorCS", {"start": v(-7.5, -2.33) * mm, "end": v(-7.62, -2.55) * mm});
            skLineSegment(sketch, "E126.MirrorCS", {"start": v(-6.73, -2.33) * mm, "end": v(-6.86, -2.55) * mm});
            skLineSegment(sketch, "E127.MirrorCS", {"start": v(4.57, -2.55) * mm, "end": v(4.45, -2.33) * mm});
            skLineSegment(sketch, "E128.MirrorCS", {"start": v(1.9, -2.33) * mm, "end": v(1.78, -2.55) * mm});
            skLineSegment(sketch, "E129.MirrorCS", {"start": v(-11.43, -2.55) * mm, "end": v(-11.56, -2.33) * mm});
            skLineSegment(sketch, "E130.MirrorCS", {"start": v(-14.6, -2.33) * mm, "end": v(-14.73, -2.55) * mm});
            skLineSegment(sketch, "E131.MirrorCS", {"start": v(1.52, -2.55) * mm, "end": v(1.4, -2.33) * mm});
            skLineSegment(sketch, "E132.MirrorCS", {"start": v(3.56, -2.55) * mm, "end": v(3.43, -2.33) * mm});
            skLineSegment(sketch, "E133.MirrorCS", {"start": v(-12.2, -2.55) * mm, "end": v(-12.32, -2.33) * mm});
            skLineSegment(sketch, "E134.MirrorCS", {"start": v(-12.57, -2.33) * mm, "end": v(-12.7, -2.55) * mm});
            skLineSegment(sketch, "E135.MirrorCS", {"start": v(-0.76, -2.55) * mm, "end": v(-0.89, -2.33) * mm});
            skLineSegment(sketch, "E136.MirrorCS", {"start": v(0, -2.55) * mm, "end": v(-0.13, -2.33) * mm});
            skLineSegment(sketch, "E137.MirrorCS", {"start": v(2.67, -2.33) * mm, "end": v(2.54, -2.55) * mm});
            skLineSegment(sketch, "E138.MirrorCS", {"start": v(5.46, -2.33) * mm, "end": v(5.33, -2.55) * mm});
            skLineSegment(sketch, "E139.MirrorCS", {"start": v(-13.34, -2.33) * mm, "end": v(-13.46, -2.55) * mm});
            skLineSegment(sketch, "E140.MirrorCS", {"start": v(1.02, -2.55) * mm, "end": v(0.89, -2.33) * mm});
            skLineSegment(sketch, "E141.MirrorCS", {"start": v(-1.65, -2.33) * mm, "end": v(-1.78, -2.55) * mm});
            skLineSegment(sketch, "E142.MirrorCS", {"start": v(-8.9, -2.55) * mm, "end": v(-9.02, -2.33) * mm});
            skLineSegment(sketch, "E143.MirrorCS", {"start": v(-18.42, -2.33) * mm, "end": v(-18.54, -2.55) * mm});
            skLineSegment(sketch, "E144.MirrorCS", {"start": v(-18.8, -2.55) * mm, "end": v(-18.92, -2.33) * mm});
            skLineSegment(sketch, "E145.MirrorCS", {"start": v(2.41, -2.33) * mm, "end": v(2.29, -2.55) * mm});
            skLineSegment(sketch, "E146.MirrorCS", {"start": v(-9.27, -2.33) * mm, "end": v(-9.4, -2.55) * mm});
            skLineSegment(sketch, "E147.MirrorCS", {"start": v(5.2, -2.33) * mm, "end": v(5.08, -2.55) * mm});
            skLineSegment(sketch, "E148.MirrorCS", {"start": v(-9.9, -2.55) * mm, "end": v(-10.03, -2.33) * mm});
            skLineSegment(sketch, "E149.MirrorCS", {"start": v(1.27, -2.55) * mm, "end": v(1.14, -2.33) * mm});
            skLineSegment(sketch, "E150.MirrorCS", {"start": v(-16.26, -2.55) * mm, "end": v(-16.38, -2.33) * mm});
            skLineSegment(sketch, "E151.MirrorCS", {"start": v(3.43, -2.33) * mm, "end": v(3.3, -2.55) * mm});
            skLineSegment(sketch, "E152.MirrorCS", {"start": v(-10.29, -2.33) * mm, "end": v(-10.41, -2.55) * mm});
            skLineSegment(sketch, "E153.MirrorCS", {"start": v(-14.86, -2.33) * mm, "end": v(-14.99, -2.55) * mm});
            skLineSegment(sketch, "E154.MirrorCS", {"start": v(-5.84, -2.55) * mm, "end": v(-5.97, -2.33) * mm});
            skLineSegment(sketch, "E155.MirrorCS", {"start": v(1.4, -2.33) * mm, "end": v(1.27, -2.55) * mm});
            skLineSegment(sketch, "E156.MirrorCS", {"start": v(4.06, -2.55) * mm, "end": v(3.94, -2.33) * mm});
            skLineSegment(sketch, "E157.MirrorCS", {"start": v(-17.27, -2.55) * mm, "end": v(-17.4, -2.33) * mm});
            skLineSegment(sketch, "E158.MirrorCS", {"start": v(-13.84, -2.33) * mm, "end": v(-13.97, -2.55) * mm});
            skLineSegment(sketch, "E159.MirrorCS", {"start": v(5.33, -2.55) * mm, "end": v(5.2, -2.33) * mm});
            skLineSegment(sketch, "E160.MirrorCS", {"start": v(-7.37, -2.55) * mm, "end": v(-7.5, -2.33) * mm});
            skLineSegment(sketch, "E161.MirrorCS", {"start": v(-13.59, -2.33) * mm, "end": v(-13.72, -2.55) * mm});
            skLineSegment(sketch, "E162.MirrorCS", {"start": v(-15.75, -2.55) * mm, "end": v(-15.88, -2.33) * mm});
            skLineSegment(sketch, "E163.MirrorCS", {"start": v(-6.48, -2.33) * mm, "end": v(-6.6, -2.55) * mm});
            skLineSegment(sketch, "E164.MirrorCS", {"start": v(-7.11, -2.55) * mm, "end": v(-7.24, -2.33) * mm});
            skLineSegment(sketch, "E165.MirrorCS", {"start": v(-7.62, -2.55) * mm, "end": v(-7.75, -2.33) * mm});
            skLineSegment(sketch, "E166.MirrorCS", {"start": v(5.59, -2.55) * mm, "end": v(5.46, -2.33) * mm});
            skLineSegment(sketch, "E167.MirrorCS", {"start": v(-13.72, -2.55) * mm, "end": v(-13.84, -2.33) * mm});
            skLineSegment(sketch, "E168.MirrorCS", {"start": v(-4.95, -2.33) * mm, "end": v(-5.08, -2.55) * mm});
            skLineSegment(sketch, "E169.MirrorCS", {"start": v(-10.92, -2.55) * mm, "end": v(-11.05, -2.33) * mm});
            skLineSegment(sketch, "E170.MirrorCS", {"start": v(-13.2, -2.55) * mm, "end": v(-13.34, -2.33) * mm});
            skLineSegment(sketch, "E171.MirrorCS", {"start": v(-17.4, -2.33) * mm, "end": v(-17.53, -2.55) * mm});
            skLineSegment(sketch, "E172.MirrorCS", {"start": v(-9.65, -2.55) * mm, "end": v(-9.78, -2.33) * mm});
            skLineSegment(sketch, "E173.MirrorCS", {"start": v(-12.07, -2.33) * mm, "end": v(-12.2, -2.55) * mm});
            skLineSegment(sketch, "E174.MirrorCS", {"start": v(-0.38, -2.33) * mm, "end": v(-0.5, -2.55) * mm});
            skLineSegment(sketch, "E175.MirrorCS", {"start": v(-4.83, -2.55) * mm, "end": v(-4.95, -2.33) * mm});
            skLineSegment(sketch, "E176.MirrorCS", {"start": v(-0.89, -2.33) * mm, "end": v(-1.02, -2.55) * mm});
            skLineSegment(sketch, "E177.MirrorCS", {"start": v(-16.13, -2.33) * mm, "end": v(-16.26, -2.55) * mm});
            skLineSegment(sketch, "E178.MirrorCS", {"start": v(-6.1, -2.55) * mm, "end": v(-6.22, -2.33) * mm});
            skLineSegment(sketch, "E179.MirrorCS", {"start": v(0.5, -2.55) * mm, "end": v(0.38, -2.33) * mm});
            skLineSegment(sketch, "E180.MirrorCS", {"start": v(-5.72, -2.33) * mm, "end": v(-5.84, -2.55) * mm});
            skLineSegment(sketch, "E181.MirrorCS", {"start": v(-14.73, -2.55) * mm, "end": v(-14.86, -2.33) * mm});
            skLineSegment(sketch, "E182.MirrorCS", {"start": v(-4.2, -2.33) * mm, "end": v(-4.32, -2.55) * mm});
            skLineSegment(sketch, "E183.MirrorCS", {"start": v(-18.92, -2.33) * mm, "end": v(-19.05, -2.55) * mm});
            skLineSegment(sketch, "E184.MirrorCS", {"start": v(-18.29, -2.55) * mm, "end": v(-18.42, -2.33) * mm});
            skLineSegment(sketch, "E185.MirrorCS", {"start": v(-2.03, -2.55) * mm, "end": v(-2.16, -2.33) * mm});
            skLineSegment(sketch, "E186.MirrorCS", {"start": v(0.63, -2.33) * mm, "end": v(0.5, -2.55) * mm});
            skLineSegment(sketch, "E187.MirrorCS", {"start": v(-0.25, -2.55) * mm, "end": v(-0.38, -2.33) * mm});
            skLineSegment(sketch, "E188.MirrorCS", {"start": v(-4.32, -2.55) * mm, "end": v(-4.45, -2.33) * mm});
            skLineSegment(sketch, "E189.MirrorCS", {"start": v(-10.16, -2.55) * mm, "end": v(-10.29, -2.33) * mm});
            skLineSegment(sketch, "E190.MirrorCS", {"start": v(-8.26, -2.33) * mm, "end": v(-8.38, -2.55) * mm});
            skLineSegment(sketch, "E191.MirrorCS", {"start": v(4.32, -2.55) * mm, "end": v(4.2, -2.33) * mm});
            skLineSegment(sketch, "E192.MirrorCS", {"start": v(0.13, -2.33) * mm, "end": v(0, -2.55) * mm});
            skLineSegment(sketch, "E193.MirrorCS", {"start": v(-4.06, -2.55) * mm, "end": v(-4.2, -2.33) * mm});
            skLineSegment(sketch, "E194.MirrorCS", {"start": v(5.72, -2.33) * mm, "end": v(5.59, -2.55) * mm});
            skLineSegment(sketch, "E195.MirrorCS", {"start": v(-1.27, -2.55) * mm, "end": v(-1.4, -2.33) * mm});
            skLineSegment(sketch, "E196.MirrorCS", {"start": v(-11.18, -2.55) * mm, "end": v(-11.3, -2.33) * mm});
            skLineSegment(sketch, "E197.MirrorCS", {"start": v(2.54, -2.55) * mm, "end": v(2.41, -2.33) * mm});
            skLineSegment(sketch, "E198.MirrorCS", {"start": v(-18.67, -2.33) * mm, "end": v(-18.8, -2.55) * mm});
            skLineSegment(sketch, "E199.MirrorCS", {"start": v(-17.9, -2.33) * mm, "end": v(-18.03, -2.55) * mm});
            skLineSegment(sketch, "E200.MirrorCS", {"start": v(-6.86, -2.55) * mm, "end": v(-6.99, -2.33) * mm});
            skLineSegment(sketch, "E201.MirrorCS", {"start": v(-17.78, -2.55) * mm, "end": v(-17.9, -2.33) * mm});
            skLineSegment(sketch, "E202.MirrorCS", {"start": v(-6.6, -2.55) * mm, "end": v(-6.73, -2.33) * mm});
            skLineSegment(sketch, "E203.MirrorCS", {"start": v(-7.87, -2.55) * mm, "end": v(-8, -2.33) * mm});
            skLineSegment(sketch, "E204.MirrorCS", {"start": v(-1.52, -2.55) * mm, "end": v(-1.65, -2.33) * mm});
            skLineSegment(sketch, "E205.MirrorCS", {"start": v(-5.2, -2.33) * mm, "end": v(-5.33, -2.55) * mm});
            skLineSegment(sketch, "E206.MirrorCS", {"start": v(-5.46, -2.33) * mm, "end": v(-5.59, -2.55) * mm});
            skLineSegment(sketch, "E207.MirrorCS", {"start": v(-1.4, -2.33) * mm, "end": v(-1.52, -2.55) * mm});
            skLineSegment(sketch, "E208.MirrorCS", {"start": v(-16, -2.55) * mm, "end": v(-16.13, -2.33) * mm});
            skLineSegment(sketch, "E209.1.0.0", {"start": v(6.48, -2.33) * mm, "end": v(6.35, -2.55) * mm});
            skLineSegment(sketch, "E209.1.0.1", {"start": v(6.6, -2.55) * mm, "end": v(6.48, -2.33) * mm});
            skLineSegment(sketch, "E209.1.0.2", {"start": v(6.48, 2.32) * mm, "end": v(6.35, 2.54) * mm});
            skLineSegment(sketch, "E209.1.0.3", {"start": v(6.6, 2.54) * mm, "end": v(6.48, 2.32) * mm});
            skLineSegment(sketch, "E209.2.0.0", {"start": v(6.73, -2.33) * mm, "end": v(6.6, -2.55) * mm});
            skLineSegment(sketch, "E209.2.0.1", {"start": v(6.86, -2.55) * mm, "end": v(6.73, -2.33) * mm});
            skLineSegment(sketch, "E209.2.0.2", {"start": v(6.73, 2.32) * mm, "end": v(6.6, 2.54) * mm});
            skLineSegment(sketch, "E209.2.0.3", {"start": v(6.86, 2.54) * mm, "end": v(6.73, 2.32) * mm});
            skLineSegment(sketch, "E209.3.0.0", {"start": v(6.99, -2.33) * mm, "end": v(6.86, -2.55) * mm});
            skLineSegment(sketch, "E209.3.0.1", {"start": v(7.11, -2.55) * mm, "end": v(6.99, -2.33) * mm});
            skLineSegment(sketch, "E209.3.0.2", {"start": v(6.99, 2.32) * mm, "end": v(6.86, 2.54) * mm});
            skLineSegment(sketch, "E209.3.0.3", {"start": v(7.11, 2.54) * mm, "end": v(6.99, 2.32) * mm});
            skLineSegment(sketch, "E209.4.0.0", {"start": v(7.24, -2.33) * mm, "end": v(7.11, -2.55) * mm});
            skLineSegment(sketch, "E209.4.0.1", {"start": v(7.37, -2.55) * mm, "end": v(7.24, -2.33) * mm});
            skLineSegment(sketch, "E209.4.0.2", {"start": v(7.24, 2.32) * mm, "end": v(7.11, 2.54) * mm});
            skLineSegment(sketch, "E209.4.0.3", {"start": v(7.37, 2.54) * mm, "end": v(7.24, 2.32) * mm});
            skLineSegment(sketch, "E209.5.0.0", {"start": v(7.5, -2.33) * mm, "end": v(7.37, -2.55) * mm});
            skLineSegment(sketch, "E209.5.0.1", {"start": v(7.62, -2.55) * mm, "end": v(7.5, -2.33) * mm});
            skLineSegment(sketch, "E209.5.0.2", {"start": v(7.5, 2.32) * mm, "end": v(7.37, 2.54) * mm});
            skLineSegment(sketch, "E209.5.0.3", {"start": v(7.62, 2.54) * mm, "end": v(7.5, 2.32) * mm});
            skLineSegment(sketch, "E209.6.0.0", {"start": v(7.75, -2.33) * mm, "end": v(7.62, -2.55) * mm});
            skLineSegment(sketch, "E209.6.0.1", {"start": v(7.87, -2.55) * mm, "end": v(7.75, -2.33) * mm});
            skLineSegment(sketch, "E209.6.0.2", {"start": v(7.75, 2.32) * mm, "end": v(7.62, 2.54) * mm});
            skLineSegment(sketch, "E209.6.0.3", {"start": v(7.87, 2.54) * mm, "end": v(7.75, 2.32) * mm});
            skLineSegment(sketch, "E209.7.0.0", {"start": v(8, -2.33) * mm, "end": v(7.87, -2.55) * mm});
            skLineSegment(sketch, "E209.7.0.1", {"start": v(8.13, -2.55) * mm, "end": v(8, -2.33) * mm});
            skLineSegment(sketch, "E209.7.0.2", {"start": v(8, 2.32) * mm, "end": v(7.87, 2.54) * mm});
            skLineSegment(sketch, "E209.7.0.3", {"start": v(8.13, 2.54) * mm, "end": v(8, 2.32) * mm});
            skLineSegment(sketch, "E209.8.0.0", {"start": v(8.26, -2.33) * mm, "end": v(8.13, -2.55) * mm});
            skLineSegment(sketch, "E209.8.0.1", {"start": v(8.38, -2.55) * mm, "end": v(8.26, -2.33) * mm});
            skLineSegment(sketch, "E209.8.0.2", {"start": v(8.26, 2.32) * mm, "end": v(8.13, 2.54) * mm});
            skLineSegment(sketch, "E209.8.0.3", {"start": v(8.38, 2.54) * mm, "end": v(8.26, 2.32) * mm});
            skLineSegment(sketch, "E209.9.0.0", {"start": v(8.5, -2.33) * mm, "end": v(8.38, -2.55) * mm});
            skLineSegment(sketch, "E209.9.0.1", {"start": v(8.64, -2.55) * mm, "end": v(8.5, -2.33) * mm});
            skLineSegment(sketch, "E209.9.0.2", {"start": v(8.5, 2.32) * mm, "end": v(8.38, 2.54) * mm});
            skLineSegment(sketch, "E209.9.0.3", {"start": v(8.64, 2.54) * mm, "end": v(8.5, 2.32) * mm});
            skLineSegment(sketch, "E209.10.0.0", {"start": v(8.76, -2.33) * mm, "end": v(8.64, -2.55) * mm});
            skLineSegment(sketch, "E209.10.0.1", {"start": v(8.9, -2.55) * mm, "end": v(8.76, -2.33) * mm});
            skLineSegment(sketch, "E209.10.0.2", {"start": v(8.76, 2.32) * mm, "end": v(8.64, 2.54) * mm});
            skLineSegment(sketch, "E209.10.0.3", {"start": v(8.9, 2.54) * mm, "end": v(8.76, 2.32) * mm});
            skLineSegment(sketch, "E209.11.0.0", {"start": v(9.02, -2.33) * mm, "end": v(8.89, -2.55) * mm});
            skLineSegment(sketch, "E209.11.0.1", {"start": v(9.14, -2.55) * mm, "end": v(9.02, -2.33) * mm});
            skLineSegment(sketch, "E209.11.0.2", {"start": v(9.02, 2.32) * mm, "end": v(8.89, 2.54) * mm});
            skLineSegment(sketch, "E209.11.0.3", {"start": v(9.14, 2.54) * mm, "end": v(9.02, 2.32) * mm});
            skLineSegment(sketch, "E209.12.0.0", {"start": v(9.27, -2.33) * mm, "end": v(9.14, -2.55) * mm});
            skLineSegment(sketch, "E209.12.0.1", {"start": v(9.4, -2.55) * mm, "end": v(9.27, -2.33) * mm});
            skLineSegment(sketch, "E209.12.0.2", {"start": v(9.27, 2.32) * mm, "end": v(9.14, 2.54) * mm});
            skLineSegment(sketch, "E209.12.0.3", {"start": v(9.4, 2.54) * mm, "end": v(9.27, 2.32) * mm});
            skLineSegment(sketch, "E209.13.0.0", {"start": v(9.53, -2.33) * mm, "end": v(9.4, -2.55) * mm});
            skLineSegment(sketch, "E209.13.0.1", {"start": v(9.65, -2.55) * mm, "end": v(9.53, -2.33) * mm});
            skLineSegment(sketch, "E209.13.0.2", {"start": v(9.53, 2.32) * mm, "end": v(9.4, 2.54) * mm});
            skLineSegment(sketch, "E209.13.0.3", {"start": v(9.65, 2.54) * mm, "end": v(9.53, 2.32) * mm});
            skLineSegment(sketch, "E209.14.0.0", {"start": v(9.78, -2.33) * mm, "end": v(9.65, -2.55) * mm});
            skLineSegment(sketch, "E209.14.0.1", {"start": v(9.9, -2.55) * mm, "end": v(9.78, -2.33) * mm});
            skLineSegment(sketch, "E209.14.0.2", {"start": v(9.78, 2.32) * mm, "end": v(9.65, 2.54) * mm});
            skLineSegment(sketch, "E209.14.0.3", {"start": v(9.9, 2.54) * mm, "end": v(9.78, 2.32) * mm});
            skLineSegment(sketch, "E209.15.0.0", {"start": v(10.03, -2.33) * mm, "end": v(9.9, -2.55) * mm});
            skLineSegment(sketch, "E209.15.0.1", {"start": v(10.16, -2.55) * mm, "end": v(10.03, -2.33) * mm});
            skLineSegment(sketch, "E209.15.0.2", {"start": v(10.03, 2.32) * mm, "end": v(9.9, 2.54) * mm});
            skLineSegment(sketch, "E209.15.0.3", {"start": v(10.16, 2.54) * mm, "end": v(10.03, 2.32) * mm});
            skLineSegment(sketch, "E209.16.0.0", {"start": v(10.29, -2.33) * mm, "end": v(10.16, -2.55) * mm});
            skLineSegment(sketch, "E209.16.0.1", {"start": v(10.41, -2.55) * mm, "end": v(10.29, -2.33) * mm});
            skLineSegment(sketch, "E209.16.0.2", {"start": v(10.29, 2.32) * mm, "end": v(10.16, 2.54) * mm});
            skLineSegment(sketch, "E209.16.0.3", {"start": v(10.41, 2.54) * mm, "end": v(10.29, 2.32) * mm});
            skLineSegment(sketch, "E209.17.0.0", {"start": v(10.54, -2.33) * mm, "end": v(10.41, -2.55) * mm});
            skLineSegment(sketch, "E209.17.0.1", {"start": v(10.67, -2.55) * mm, "end": v(10.54, -2.33) * mm});
            skLineSegment(sketch, "E209.17.0.2", {"start": v(10.54, 2.32) * mm, "end": v(10.41, 2.54) * mm});
            skLineSegment(sketch, "E209.17.0.3", {"start": v(10.67, 2.54) * mm, "end": v(10.54, 2.32) * mm});
            skLineSegment(sketch, "E209.18.0.0", {"start": v(10.8, -2.33) * mm, "end": v(10.67, -2.55) * mm});
            skLineSegment(sketch, "E209.18.0.1", {"start": v(10.92, -2.55) * mm, "end": v(10.8, -2.33) * mm});
            skLineSegment(sketch, "E209.18.0.2", {"start": v(10.8, 2.32) * mm, "end": v(10.67, 2.54) * mm});
            skLineSegment(sketch, "E209.18.0.3", {"start": v(10.92, 2.54) * mm, "end": v(10.8, 2.32) * mm});
            skLineSegment(sketch, "E209.19.0.0", {"start": v(11.05, -2.33) * mm, "end": v(10.92, -2.55) * mm});
            skLineSegment(sketch, "E209.19.0.1", {"start": v(11.18, -2.55) * mm, "end": v(11.05, -2.33) * mm});
            skLineSegment(sketch, "E209.19.0.2", {"start": v(11.05, 2.32) * mm, "end": v(10.92, 2.54) * mm});
            skLineSegment(sketch, "E209.19.0.3", {"start": v(11.18, 2.54) * mm, "end": v(11.05, 2.32) * mm});
            skLineSegment(sketch, "E209.20.0.0", {"start": v(11.3, -2.33) * mm, "end": v(11.18, -2.55) * mm});
            skLineSegment(sketch, "E209.20.0.1", {"start": v(11.43, -2.55) * mm, "end": v(11.3, -2.33) * mm});
            skLineSegment(sketch, "E209.20.0.2", {"start": v(11.3, 2.32) * mm, "end": v(11.18, 2.54) * mm});
            skLineSegment(sketch, "E209.20.0.3", {"start": v(11.43, 2.54) * mm, "end": v(11.3, 2.32) * mm});
            skLineSegment(sketch, "E209.21.0.0", {"start": v(11.56, -2.33) * mm, "end": v(11.43, -2.55) * mm});
            skLineSegment(sketch, "E209.21.0.1", {"start": v(11.68, -2.55) * mm, "end": v(11.56, -2.33) * mm});
            skLineSegment(sketch, "E209.21.0.2", {"start": v(11.56, 2.32) * mm, "end": v(11.43, 2.54) * mm});
            skLineSegment(sketch, "E209.21.0.3", {"start": v(11.68, 2.54) * mm, "end": v(11.56, 2.32) * mm});
            skLineSegment(sketch, "E209.22.0.0", {"start": v(11.81, -2.33) * mm, "end": v(11.68, -2.55) * mm});
            skLineSegment(sketch, "E209.22.0.1", {"start": v(11.94, -2.55) * mm, "end": v(11.81, -2.33) * mm});
            skLineSegment(sketch, "E209.22.0.2", {"start": v(11.81, 2.32) * mm, "end": v(11.68, 2.54) * mm});
            skLineSegment(sketch, "E209.22.0.3", {"start": v(11.94, 2.54) * mm, "end": v(11.81, 2.32) * mm});
            skLineSegment(sketch, "E209.23.0.0", {"start": v(12.06, -2.33) * mm, "end": v(11.94, -2.55) * mm});
            skLineSegment(sketch, "E209.23.0.1", {"start": v(12.2, -2.55) * mm, "end": v(12.06, -2.33) * mm});
            skLineSegment(sketch, "E209.23.0.2", {"start": v(12.06, 2.32) * mm, "end": v(11.94, 2.54) * mm});
            skLineSegment(sketch, "E209.23.0.3", {"start": v(12.2, 2.54) * mm, "end": v(12.06, 2.32) * mm});
            skLineSegment(sketch, "E209.24.0.0", {"start": v(12.32, -2.33) * mm, "end": v(12.2, -2.55) * mm});
            skLineSegment(sketch, "E209.24.0.1", {"start": v(12.45, -2.55) * mm, "end": v(12.32, -2.33) * mm});
            skLineSegment(sketch, "E209.24.0.2", {"start": v(12.32, 2.32) * mm, "end": v(12.2, 2.54) * mm});
            skLineSegment(sketch, "E209.24.0.3", {"start": v(12.45, 2.54) * mm, "end": v(12.32, 2.32) * mm});
            skLineSegment(sketch, "E209.direction1", {"start": v(6.1, -2.55) * mm, "end": v(6.35, -2.55) * mm, "construction": true});
            skLineSegment(sketch, "E210.1.0.0", {"start": v(12.57, 2.32) * mm, "end": v(12.45, 2.54) * mm});
            skLineSegment(sketch, "E210.1.0.1", {"start": v(12.7, 2.54) * mm, "end": v(12.57, 2.32) * mm});
            skLineSegment(sketch, "E210.1.0.2", {"start": v(12.7, -2.55) * mm, "end": v(12.57, -2.33) * mm});
            skLineSegment(sketch, "E210.1.0.3", {"start": v(12.57, -2.33) * mm, "end": v(12.45, -2.55) * mm});
            skLineSegment(sketch, "E210.2.0.0", {"start": v(12.83, 2.32) * mm, "end": v(12.7, 2.54) * mm});
            skLineSegment(sketch, "E210.2.0.1", {"start": v(12.95, 2.54) * mm, "end": v(12.83, 2.32) * mm});
            skLineSegment(sketch, "E210.2.0.2", {"start": v(12.95, -2.55) * mm, "end": v(12.83, -2.33) * mm});
            skLineSegment(sketch, "E210.2.0.3", {"start": v(12.83, -2.33) * mm, "end": v(12.7, -2.55) * mm});
            skLineSegment(sketch, "E210.3.0.0", {"start": v(13.08, 2.32) * mm, "end": v(12.95, 2.54) * mm});
            skLineSegment(sketch, "E210.3.0.1", {"start": v(13.2, 2.54) * mm, "end": v(13.08, 2.32) * mm});
            skLineSegment(sketch, "E210.3.0.2", {"start": v(13.2, -2.55) * mm, "end": v(13.08, -2.33) * mm});
            skLineSegment(sketch, "E210.3.0.3", {"start": v(13.08, -2.33) * mm, "end": v(12.95, -2.55) * mm});
            skLineSegment(sketch, "E210.4.0.0", {"start": v(13.34, 2.32) * mm, "end": v(13.2, 2.54) * mm});
            skLineSegment(sketch, "E210.4.0.1", {"start": v(13.46, 2.54) * mm, "end": v(13.34, 2.32) * mm});
            skLineSegment(sketch, "E210.4.0.2", {"start": v(13.46, -2.55) * mm, "end": v(13.34, -2.33) * mm});
            skLineSegment(sketch, "E210.4.0.3", {"start": v(13.34, -2.33) * mm, "end": v(13.2, -2.55) * mm});
            skLineSegment(sketch, "E210.5.0.0", {"start": v(13.59, 2.32) * mm, "end": v(13.46, 2.54) * mm});
            skLineSegment(sketch, "E210.5.0.1", {"start": v(13.72, 2.54) * mm, "end": v(13.59, 2.32) * mm});
            skLineSegment(sketch, "E210.5.0.2", {"start": v(13.72, -2.55) * mm, "end": v(13.59, -2.33) * mm});
            skLineSegment(sketch, "E210.5.0.3", {"start": v(13.59, -2.33) * mm, "end": v(13.46, -2.55) * mm});
            skLineSegment(sketch, "E210.6.0.0", {"start": v(13.84, 2.32) * mm, "end": v(13.72, 2.54) * mm});
            skLineSegment(sketch, "E210.6.0.1", {"start": v(13.97, 2.54) * mm, "end": v(13.84, 2.32) * mm});
            skLineSegment(sketch, "E210.6.0.2", {"start": v(13.97, -2.55) * mm, "end": v(13.84, -2.33) * mm});
            skLineSegment(sketch, "E210.6.0.3", {"start": v(13.84, -2.33) * mm, "end": v(13.72, -2.55) * mm});
            skLineSegment(sketch, "E210.7.0.0", {"start": v(14.1, 2.32) * mm, "end": v(13.97, 2.54) * mm});
            skLineSegment(sketch, "E210.7.0.1", {"start": v(14.22, 2.54) * mm, "end": v(14.1, 2.32) * mm});
            skLineSegment(sketch, "E210.7.0.2", {"start": v(14.22, -2.55) * mm, "end": v(14.1, -2.33) * mm});
            skLineSegment(sketch, "E210.7.0.3", {"start": v(14.1, -2.33) * mm, "end": v(13.97, -2.55) * mm});
            skLineSegment(sketch, "E210.8.0.0", {"start": v(14.35, 2.32) * mm, "end": v(14.22, 2.54) * mm});
            skLineSegment(sketch, "E210.8.0.1", {"start": v(14.48, 2.54) * mm, "end": v(14.35, 2.32) * mm});
            skLineSegment(sketch, "E210.8.0.2", {"start": v(14.48, -2.55) * mm, "end": v(14.35, -2.33) * mm});
            skLineSegment(sketch, "E210.8.0.3", {"start": v(14.35, -2.33) * mm, "end": v(14.22, -2.55) * mm});
            skLineSegment(sketch, "E210.9.0.0", {"start": v(14.6, 2.32) * mm, "end": v(14.48, 2.54) * mm});
            skLineSegment(sketch, "E210.9.0.1", {"start": v(14.73, 2.54) * mm, "end": v(14.6, 2.32) * mm});
            skLineSegment(sketch, "E210.9.0.2", {"start": v(14.73, -2.55) * mm, "end": v(14.6, -2.33) * mm});
            skLineSegment(sketch, "E210.9.0.3", {"start": v(14.6, -2.33) * mm, "end": v(14.48, -2.55) * mm});
            skLineSegment(sketch, "E210.10.0.0", {"start": v(14.86, 2.32) * mm, "end": v(14.73, 2.54) * mm});
            skLineSegment(sketch, "E210.10.0.1", {"start": v(14.99, 2.54) * mm, "end": v(14.86, 2.32) * mm});
            skLineSegment(sketch, "E210.10.0.2", {"start": v(14.99, -2.55) * mm, "end": v(14.86, -2.33) * mm});
            skLineSegment(sketch, "E210.10.0.3", {"start": v(14.86, -2.33) * mm, "end": v(14.73, -2.55) * mm});
            skLineSegment(sketch, "E210.11.0.0", {"start": v(15.11, 2.32) * mm, "end": v(14.99, 2.54) * mm});
            skLineSegment(sketch, "E210.11.0.1", {"start": v(15.24, 2.54) * mm, "end": v(15.11, 2.32) * mm});
            skLineSegment(sketch, "E210.11.0.2", {"start": v(15.24, -2.55) * mm, "end": v(15.11, -2.33) * mm});
            skLineSegment(sketch, "E210.11.0.3", {"start": v(15.11, -2.33) * mm, "end": v(14.99, -2.55) * mm});
            skLineSegment(sketch, "E210.12.0.0", {"start": v(15.37, 2.32) * mm, "end": v(15.24, 2.54) * mm});
            skLineSegment(sketch, "E210.12.0.1", {"start": v(15.5, 2.54) * mm, "end": v(15.37, 2.32) * mm});
            skLineSegment(sketch, "E210.12.0.2", {"start": v(15.5, -2.55) * mm, "end": v(15.37, -2.33) * mm});
            skLineSegment(sketch, "E210.12.0.3", {"start": v(15.37, -2.33) * mm, "end": v(15.24, -2.55) * mm});
            skLineSegment(sketch, "E210.13.0.0", {"start": v(15.62, 2.32) * mm, "end": v(15.5, 2.54) * mm});
            skLineSegment(sketch, "E210.13.0.1", {"start": v(15.75, 2.54) * mm, "end": v(15.62, 2.32) * mm});
            skLineSegment(sketch, "E210.13.0.2", {"start": v(15.75, -2.55) * mm, "end": v(15.62, -2.33) * mm});
            skLineSegment(sketch, "E210.13.0.3", {"start": v(15.62, -2.33) * mm, "end": v(15.5, -2.55) * mm});
            skLineSegment(sketch, "E210.14.0.0", {"start": v(15.88, 2.32) * mm, "end": v(15.75, 2.54) * mm});
            skLineSegment(sketch, "E210.14.0.1", {"start": v(16, 2.54) * mm, "end": v(15.88, 2.32) * mm});
            skLineSegment(sketch, "E210.14.0.2", {"start": v(16, -2.55) * mm, "end": v(15.88, -2.33) * mm});
            skLineSegment(sketch, "E210.14.0.3", {"start": v(15.88, -2.33) * mm, "end": v(15.75, -2.55) * mm});
            skLineSegment(sketch, "E210.15.0.0", {"start": v(16.13, 2.32) * mm, "end": v(16, 2.54) * mm});
            skLineSegment(sketch, "E210.15.0.1", {"start": v(16.26, 2.54) * mm, "end": v(16.13, 2.32) * mm});
            skLineSegment(sketch, "E210.15.0.2", {"start": v(16.26, -2.55) * mm, "end": v(16.13, -2.33) * mm});
            skLineSegment(sketch, "E210.15.0.3", {"start": v(16.13, -2.33) * mm, "end": v(16, -2.55) * mm});
            skLineSegment(sketch, "E210.16.0.0", {"start": v(16.38, 2.32) * mm, "end": v(16.26, 2.54) * mm});
            skLineSegment(sketch, "E210.16.0.1", {"start": v(16.51, 2.54) * mm, "end": v(16.38, 2.32) * mm});
            skLineSegment(sketch, "E210.16.0.2", {"start": v(16.51, -2.55) * mm, "end": v(16.38, -2.33) * mm});
            skLineSegment(sketch, "E210.16.0.3", {"start": v(16.38, -2.33) * mm, "end": v(16.26, -2.55) * mm});
            skLineSegment(sketch, "E210.17.0.0", {"start": v(16.64, 2.32) * mm, "end": v(16.51, 2.54) * mm});
            skLineSegment(sketch, "E210.17.0.1", {"start": v(16.76, 2.54) * mm, "end": v(16.64, 2.32) * mm});
            skLineSegment(sketch, "E210.17.0.2", {"start": v(16.76, -2.55) * mm, "end": v(16.64, -2.33) * mm});
            skLineSegment(sketch, "E210.17.0.3", {"start": v(16.64, -2.33) * mm, "end": v(16.51, -2.55) * mm});
            skLineSegment(sketch, "E210.18.0.0", {"start": v(16.9, 2.32) * mm, "end": v(16.76, 2.54) * mm});
            skLineSegment(sketch, "E210.18.0.1", {"start": v(17.02, 2.54) * mm, "end": v(16.9, 2.32) * mm});
            skLineSegment(sketch, "E210.18.0.2", {"start": v(17.02, -2.55) * mm, "end": v(16.9, -2.33) * mm});
            skLineSegment(sketch, "E210.18.0.3", {"start": v(16.9, -2.33) * mm, "end": v(16.76, -2.55) * mm});
            skLineSegment(sketch, "E210.19.0.0", {"start": v(17.15, 2.32) * mm, "end": v(17.02, 2.54) * mm});
            skLineSegment(sketch, "E210.19.0.1", {"start": v(17.27, 2.54) * mm, "end": v(17.15, 2.32) * mm});
            skLineSegment(sketch, "E210.19.0.2", {"start": v(17.27, -2.55) * mm, "end": v(17.15, -2.33) * mm});
            skLineSegment(sketch, "E210.19.0.3", {"start": v(17.15, -2.33) * mm, "end": v(17.02, -2.55) * mm});
            skLineSegment(sketch, "E210.20.0.0", {"start": v(17.4, 2.32) * mm, "end": v(17.27, 2.54) * mm});
            skLineSegment(sketch, "E210.20.0.1", {"start": v(17.53, 2.54) * mm, "end": v(17.4, 2.32) * mm});
            skLineSegment(sketch, "E210.20.0.2", {"start": v(17.53, -2.55) * mm, "end": v(17.4, -2.33) * mm});
            skLineSegment(sketch, "E210.20.0.3", {"start": v(17.4, -2.33) * mm, "end": v(17.27, -2.55) * mm});
            skLineSegment(sketch, "E210.21.0.0", {"start": v(17.65, 2.32) * mm, "end": v(17.53, 2.54) * mm});
            skLineSegment(sketch, "E210.21.0.1", {"start": v(17.78, 2.54) * mm, "end": v(17.65, 2.32) * mm});
            skLineSegment(sketch, "E210.21.0.2", {"start": v(17.78, -2.55) * mm, "end": v(17.65, -2.33) * mm});
            skLineSegment(sketch, "E210.21.0.3", {"start": v(17.65, -2.33) * mm, "end": v(17.53, -2.55) * mm});
            skLineSegment(sketch, "E210.22.0.0", {"start": v(17.9, 2.32) * mm, "end": v(17.78, 2.54) * mm});
            skLineSegment(sketch, "E210.22.0.1", {"start": v(18.03, 2.54) * mm, "end": v(17.9, 2.32) * mm});
            skLineSegment(sketch, "E210.22.0.2", {"start": v(18.03, -2.55) * mm, "end": v(17.9, -2.33) * mm});
            skLineSegment(sketch, "E210.22.0.3", {"start": v(17.9, -2.33) * mm, "end": v(17.78, -2.55) * mm});
            skLineSegment(sketch, "E210.23.0.0", {"start": v(18.16, 2.32) * mm, "end": v(18.03, 2.54) * mm});
            skLineSegment(sketch, "E210.23.0.1", {"start": v(18.29, 2.54) * mm, "end": v(18.16, 2.32) * mm});
            skLineSegment(sketch, "E210.23.0.2", {"start": v(18.29, -2.55) * mm, "end": v(18.16, -2.33) * mm});
            skLineSegment(sketch, "E210.23.0.3", {"start": v(18.16, -2.33) * mm, "end": v(18.03, -2.55) * mm});
            skLineSegment(sketch, "E210.24.0.0", {"start": v(18.42, 2.32) * mm, "end": v(18.29, 2.54) * mm});
            skLineSegment(sketch, "E210.24.0.1", {"start": v(18.54, 2.54) * mm, "end": v(18.42, 2.32) * mm});
            skLineSegment(sketch, "E210.24.0.2", {"start": v(18.54, -2.55) * mm, "end": v(18.42, -2.33) * mm});
            skLineSegment(sketch, "E210.24.0.3", {"start": v(18.42, -2.33) * mm, "end": v(18.29, -2.55) * mm});
            skLineSegment(sketch, "E210.direction1", {"start": v(12.2, -2.55) * mm, "end": v(12.45, -2.55) * mm, "construction": true});
            skLineSegment(sketch, "E211", {"start": v(18.54, 2.54) * mm, "end": v(18.54, 2.6) * mm});
            skLineSegment(sketch, "E212", {"start": v(18.54, -2.55) * mm, "end": v(18.54, -2.6) * mm});
            skLineSegment(sketch, "E213", {"start": v(-19.05, 2.6) * mm, "end": v(18.54, 2.6) * mm});
            skLineSegment(sketch, "E214", {"start": v(18.54, -2.6) * mm, "end": v(-19.05, -2.6) * mm});
            skSolve(sketch);
        }
        {
            var Q0;
            Q0=qSketchRegion(id+"F4",true);
            extrude(context, id + "F5", {"entities" : qUnion([Q0]), "operationType" : NewBodyOperationType.REMOVE, "endBound" : BoundingType.SYMMETRIC, "oppositeDirection" : true, "depth" : 25.4 * mm, "offsetDistance" : 25.4 * mm});
        }
        {
            var Q0;
            Q0=makeQuery(id+"F3.boolean.opBoolean","SPLIT",EDGE,{"disambiguationData":[OD(1.0)],"derivedFrom":makeQuery(id+"F1.opExtrude","CAP_EDGE",EDGE,{"disambiguationData":[OSD([sQuery(id+"F0.wireOp",EDGE,"E0")])],"isStart":false})});
            var Q1;
            Q1=makeQuery(id+"F3.boolean.opBoolean","SPLIT",EDGE,{"disambiguationData":[OD(0.0)],"derivedFrom":makeQuery(id+"F1.opExtrude","CAP_EDGE",EDGE,{"disambiguationData":[OSD([sQuery(id+"F0.wireOp",EDGE,"E0")])],"isStart":false})});
            var Q2;
            Q2=makeQuery(id+"F3.boolean.opBoolean","SPLIT",EDGE,{"disambiguationData":[OD(1.0)],"derivedFrom":makeQuery(id+"F1.opExtrude","CAP_EDGE",EDGE,{"disambiguationData":[OSD([sQuery(id+"F0.wireOp",EDGE,"E0")])],"isStart":true})});
            var Q3;
            Q3=makeQuery(id+"F3.boolean.opBoolean","SPLIT",EDGE,{"disambiguationData":[OD(0.0)],"derivedFrom":makeQuery(id+"F1.opExtrude","CAP_EDGE",EDGE,{"disambiguationData":[OSD([sQuery(id+"F0.wireOp",EDGE,"E0")])],"isStart":true})});
            var Q4;
            Q4=makeQuery(id+"F3.boolean.opBoolean","INTERSECT",EDGE,{"derivedFrom":[makeQuery(id+"F1.opExtrude","CAP_FACE",FACE,{"disambiguationData":[OSD([sQuery(id+"F0.wireOp",EDGE,"E0")])],"isStart":true}),makeQuery(id+"F3.boolean.toolComplement.opBoolean","COPY",FACE,{"derivedFrom":makeQuery(id+"F3.opExtrude","SWEPT_FACE",FACE,{"disambiguationData":[OSD([sQuery(id+"F2.wireOp",EDGE,"E1.bottom")])]})})]});
            var Q5;
            Q5=makeQuery(id+"F3.boolean.opBoolean","INTERSECT",EDGE,{"derivedFrom":[makeQuery(id+"F1.opExtrude","CAP_FACE",FACE,{"disambiguationData":[OSD([sQuery(id+"F0.wireOp",EDGE,"E0")])],"isStart":true}),makeQuery(id+"F3.boolean.toolComplement.opBoolean","COPY",FACE,{"derivedFrom":makeQuery(id+"F3.opExtrude","SWEPT_FACE",FACE,{"disambiguationData":[OSD([sQuery(id+"F2.wireOp",EDGE,"E1.top")])]})})]});
            fillet(context, id + "F6", {"entities" : qUnion([Q0, Q1, Q2, Q3, Q4, Q5]), "radius" : 0.25 * mm, "tangentPropagation" : true, "allowEdgeOverflow" : false});
        }
        {
            var Q0;
            Q0=makeQuery(id+"F1.opExtrude","CAP_FACE",FACE,{"disambiguationData":[OSD([sQuery(id+"F0.wireOp",EDGE,"E0")])],"isStart":true});
            var sketch = newSketch(context, id + "F7", { "sketchPlane" : qUnion([Q0])});
            skLineSegment(sketch, "E215.bottom", {"start": v(9.27, -0.63) * mm, "end": v(7.62, -0.63) * mm});
            skLineSegment(sketch, "E215.top", {"start": v(9.27, 0.64) * mm, "end": v(7.62, 0.64) * mm});
            skLineSegment(sketch, "E215.left", {"start": v(9.53, -0.38) * mm, "end": v(9.53, 0.38) * mm});
            skLineSegment(sketch, "E215.right", {"start": v(-9.53, -0.38) * mm, "end": v(-9.53, 0.38) * mm});
            skPoint(sketch, "E215.middle", {"position": v(0, 0) * mm});
            skPoint(sketch, "E216.visualSharp", {"position": v(-9.53, 0.63) * mm});
            skArc(sketch, "E216.filletArc", {"start": v(-9.27, 0.63) * mm, "mid": v(-9.45, 0.56) * mm, "end": v(-9.53, 0.38) * mm});
            skPoint(sketch, "E217.visualSharp", {"position": v(-9.53, -0.64) * mm});
            skArc(sketch, "E217.filletArc", {"start": v(-9.53, -0.38) * mm, "mid": v(-9.45, -0.56) * mm, "end": v(-9.27, -0.64) * mm});
            skPoint(sketch, "E218.visualSharp", {"position": v(9.53, 0.64) * mm});
            skArc(sketch, "E218.filletArc", {"start": v(9.53, 0.38) * mm, "mid": v(9.45, 0.56) * mm, "end": v(9.27, 0.64) * mm});
            skPoint(sketch, "E219.visualSharp", {"position": v(9.53, -0.63) * mm});
            skArc(sketch, "E219.filletArc", {"start": v(9.27, -0.63) * mm, "mid": v(9.45, -0.56) * mm, "end": v(9.53, -0.38) * mm});
            skLineSegment(sketch, "E220.bottom", {"start": v(1.27, -2.54) * mm, "end": v(-1.27, -2.54) * mm});
            skLineSegment(sketch, "E220.top", {"start": v(1.27, 2.54) * mm, "end": v(-1.27, 2.54) * mm});
            skLineSegment(sketch, "E220.left", {"start": v(1.27, -2.54) * mm, "end": v(1.27, -0.64) * mm});
            skLineSegment(sketch, "E220.right", {"start": v(-1.27, -2.54) * mm, "end": v(-1.27, -0.64) * mm});
            skLineSegment(sketch, "E221.bottom", {"start": v(-5.08, -2.54) * mm, "end": v(-7.62, -2.54) * mm});
            skLineSegment(sketch, "E221.top", {"start": v(-5.08, 2.54) * mm, "end": v(-7.62, 2.54) * mm});
            skLineSegment(sketch, "E221.left", {"start": v(-5.08, -2.54) * mm, "end": v(-5.08, -0.64) * mm});
            skLineSegment(sketch, "E221.right", {"start": v(-7.62, -2.54) * mm, "end": v(-7.62, -0.64) * mm});
            skPoint(sketch, "E221.middle", {"position": v(-6.35, 0) * mm});
            skLineSegment(sketch, "E222.bottom", {"start": v(7.62, -2.54) * mm, "end": v(5.08, -2.54) * mm});
            skLineSegment(sketch, "E222.top", {"start": v(7.62, 2.54) * mm, "end": v(5.08, 2.54) * mm});
            skLineSegment(sketch, "E222.left", {"start": v(7.62, -2.54) * mm, "end": v(7.62, -0.63) * mm});
            skLineSegment(sketch, "E222.right", {"start": v(5.08, -2.54) * mm, "end": v(5.08, -0.63) * mm});
            skPoint(sketch, "E222.middle", {"position": v(6.35, 0) * mm});
            skLineSegment(sketch, "E223.trimOffspring", {"start": v(-7.62, 0.63) * mm, "end": v(-7.62, 2.54) * mm});
            skLineSegment(sketch, "E224.trimOffspring", {"start": v(-7.62, 0.63) * mm, "end": v(-9.27, 0.63) * mm});
            skLineSegment(sketch, "E225.trimOffspring", {"start": v(-5.08, 0.64) * mm, "end": v(-5.08, 2.54) * mm});
            skLineSegment(sketch, "E226.trimOffspring", {"start": v(-7.62, -0.64) * mm, "end": v(-9.27, -0.64) * mm});
            skLineSegment(sketch, "E227.trimOffspring", {"start": v(-1.27, 0.64) * mm, "end": v(-1.27, 2.54) * mm});
            skLineSegment(sketch, "E228.trimOffspring", {"start": v(-1.27, 0.64) * mm, "end": v(-5.08, 0.64) * mm});
            skLineSegment(sketch, "E229.trimOffspring", {"start": v(-1.27, -0.64) * mm, "end": v(-5.08, -0.64) * mm});
            skLineSegment(sketch, "E230.trimOffspring", {"start": v(1.27, 0.64) * mm, "end": v(1.27, 2.54) * mm});
            skLineSegment(sketch, "E231.trimOffspring", {"start": v(5.08, 0.64) * mm, "end": v(1.27, 0.64) * mm});
            skLineSegment(sketch, "E232.trimOffspring", {"start": v(5.08, -0.63) * mm, "end": v(1.27, -0.64) * mm});
            skLineSegment(sketch, "E233.trimOffspring", {"start": v(5.08, 0.64) * mm, "end": v(5.08, 2.54) * mm});
            skLineSegment(sketch, "E234.trimOffspring", {"start": v(7.62, 0.64) * mm, "end": v(7.62, 2.54) * mm});
            skSolve(sketch);
        }
        {
            var Q0;
            Q0 = qSketchRegion(id + "F7", true);
            extrude(context, id + "F8", {"entities" : qUnion([Q0]), "operationType" : NewBodyOperationType.REMOVE, "oppositeDirection" : true, "depth" : 0.5 * mm, "offsetDistance" : 25.4 * mm});
        }
    });
